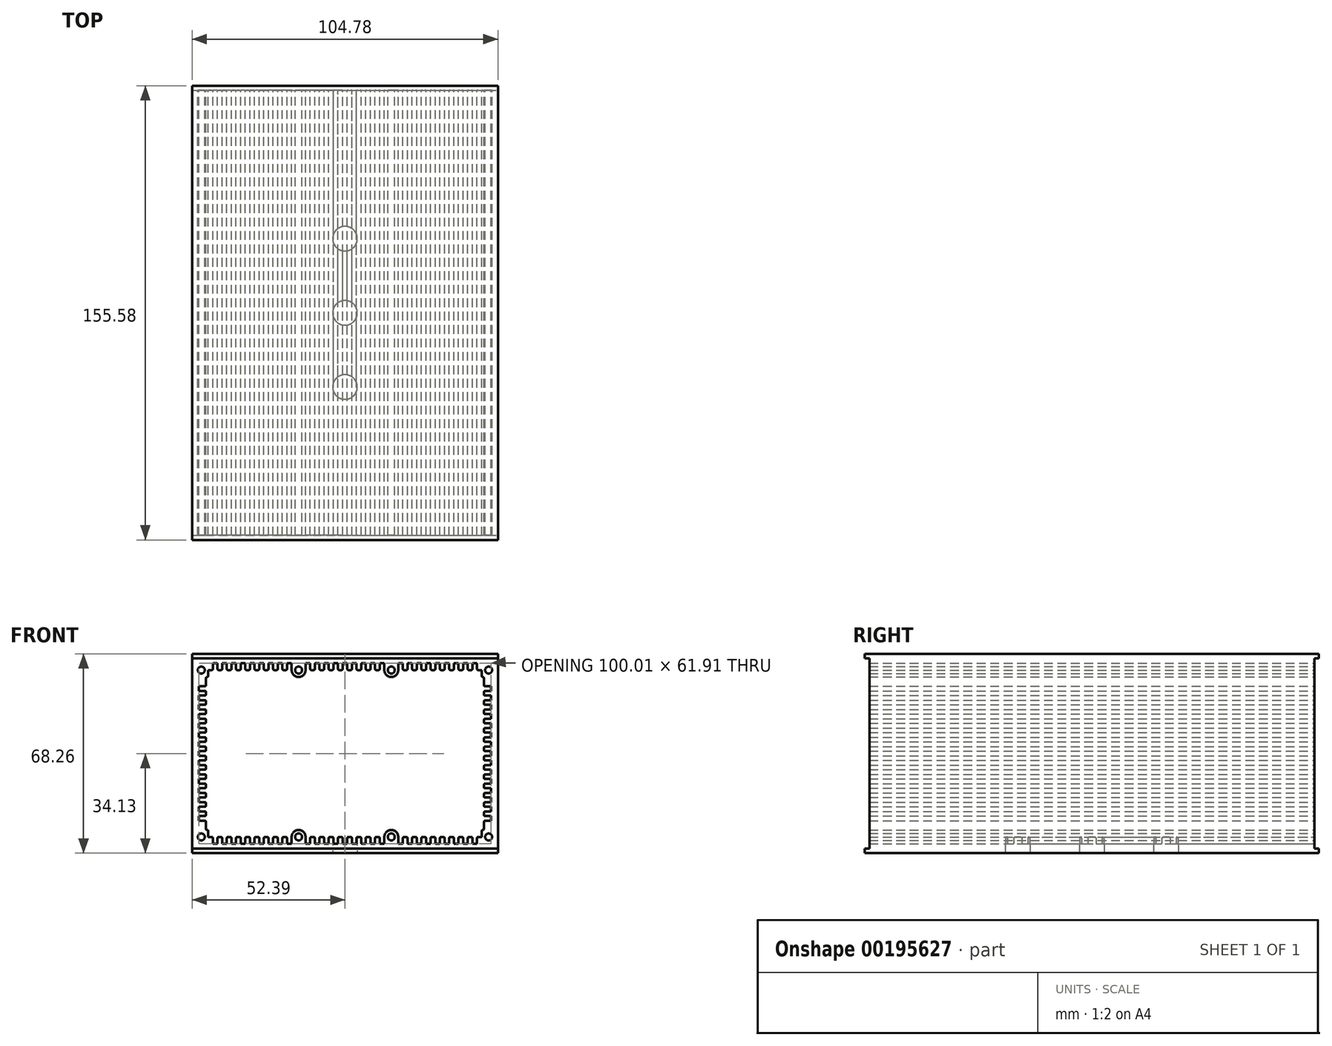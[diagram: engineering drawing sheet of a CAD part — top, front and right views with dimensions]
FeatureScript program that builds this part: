
annotation { "Feature Type Name" : "Feature", "Feature Type Description" : "" }
export const myFeature = defineFeature(function(context is Context, id is Id, definition is map)
    precondition{}
    {
        {
            var Q0;
            Q0=qCreatedBy(makeId("Front.planeOp"),FACE);
            var sketch = newSketch(context, id + "F0", { "sketchPlane" : qUnion([Q0])});
            skLineSegment(sketch, "E0.bottom", {"start": v(-52.39, 34.13) * mm, "end": v(52.39, 34.13) * mm});
            skLineSegment(sketch, "E0.top", {"start": v(-52.39, -34.13) * mm, "end": v(52.39, -34.13) * mm});
            skLineSegment(sketch, "E0.left", {"start": v(-52.39, 34.13) * mm, "end": v(-52.39, -34.13) * mm});
            skLineSegment(sketch, "E0.right", {"start": v(52.39, 34.13) * mm, "end": v(52.39, -34.13) * mm});
            skLineSegment(sketch, "E1.bottom", {"start": v(-50, 23.02) * mm, "end": v(-48.02, 23.02) * mm});
            skLineSegment(sketch, "E1.top", {"start": v(-50, 21.43) * mm, "end": v(-48.02, 21.43) * mm});
            skLineSegment(sketch, "E1.left", {"start": v(-50, 23.02) * mm, "end": v(-50, 21.43) * mm});
            skLineSegment(sketch, "E2", {"start": v(-47.62, 21.03) * mm, "end": v(-47.62, 20.24) * mm});
            skLineSegment(sketch, "E3.bottom", {"start": v(-50, 19.84) * mm, "end": v(-48.02, 19.84) * mm});
            skLineSegment(sketch, "E3.top", {"start": v(-50, 18.26) * mm, "end": v(-48.02, 18.26) * mm});
            skLineSegment(sketch, "E3.left", {"start": v(-50, 19.84) * mm, "end": v(-50, 18.26) * mm});
            skLineSegment(sketch, "E4", {"start": v(-47.62, 17.86) * mm, "end": v(-47.62, 17.07) * mm});
            skLineSegment(sketch, "E5.bottom", {"start": v(-50, 16.67) * mm, "end": v(-48.02, 16.67) * mm});
            skLineSegment(sketch, "E5.top", {"start": v(-50, 15.08) * mm, "end": v(-48.02, 15.08) * mm});
            skLineSegment(sketch, "E5.left", {"start": v(-50, 16.67) * mm, "end": v(-50, 15.08) * mm});
            skLineSegment(sketch, "E6", {"start": v(-47.62, 14.68) * mm, "end": v(-47.62, 13.9) * mm});
            skLineSegment(sketch, "E7.bottom", {"start": v(-50, 13.5) * mm, "end": v(-48.02, 13.5) * mm});
            skLineSegment(sketch, "E7.top", {"start": v(-50, 11.9) * mm, "end": v(-48.02, 11.9) * mm});
            skLineSegment(sketch, "E7.left", {"start": v(-50, 13.5) * mm, "end": v(-50, 11.9) * mm});
            skLineSegment(sketch, "E8", {"start": v(-47.62, 11.5) * mm, "end": v(-47.62, 10.72) * mm});
            skLineSegment(sketch, "E9.bottom", {"start": v(-50, 10.32) * mm, "end": v(-48.02, 10.32) * mm});
            skLineSegment(sketch, "E9.top", {"start": v(-50, 8.73) * mm, "end": v(-48.02, 8.73) * mm});
            skLineSegment(sketch, "E9.left", {"start": v(-50, 10.32) * mm, "end": v(-50, 8.73) * mm});
            skLineSegment(sketch, "E10", {"start": v(-47.62, 8.33) * mm, "end": v(-47.62, 7.54) * mm});
            skLineSegment(sketch, "E11.bottom", {"start": v(-50, 7.14) * mm, "end": v(-48.02, 7.14) * mm});
            skLineSegment(sketch, "E11.top", {"start": v(-50, 5.56) * mm, "end": v(-48.02, 5.56) * mm});
            skLineSegment(sketch, "E11.left", {"start": v(-50, 7.14) * mm, "end": v(-50, 5.56) * mm});
            skLineSegment(sketch, "E12", {"start": v(-47.62, 5.16) * mm, "end": v(-47.62, 4.37) * mm});
            skLineSegment(sketch, "E13.bottom", {"start": v(-50, 3.97) * mm, "end": v(-48.02, 3.97) * mm});
            skLineSegment(sketch, "E13.top", {"start": v(-50, 2.38) * mm, "end": v(-48.02, 2.38) * mm});
            skLineSegment(sketch, "E13.left", {"start": v(-50, 3.97) * mm, "end": v(-50, 2.38) * mm});
            skLineSegment(sketch, "E14", {"start": v(-47.62, 1.98) * mm, "end": v(-47.62, 1.2) * mm});
            skLineSegment(sketch, "E15.bottom", {"start": v(-50, 0.8) * mm, "end": v(-48.02, 0.8) * mm});
            skLineSegment(sketch, "E15.left", {"start": v(-50, 0.8) * mm, "end": v(-50, 0) * mm});
            skLineSegment(sketch, "E16.bottom", {"start": v(-43.66, 30.96) * mm, "end": v(-43.66, 28.97) * mm});
            skLineSegment(sketch, "E16.top", {"start": v(-45.24, 30.96) * mm, "end": v(-45.24, 28.97) * mm});
            skLineSegment(sketch, "E16.left", {"start": v(-43.66, 30.96) * mm, "end": v(-45.24, 30.96) * mm});
            skLineSegment(sketch, "E17", {"start": v(-45.64, 28.57) * mm, "end": v(-46.83, 28.57) * mm});
            skCircle(sketch, "E18", {"center": v(-49.21, 28.58) * mm, "radius": 1.2 * mm});
            skLineSegment(sketch, "E19", {"start": v(-47.62, 23.42) * mm, "end": v(-47.62, 25.8) * mm});
            skLineSegment(sketch, "E20", {"start": v(-46.83, 28.57) * mm, "end": v(-46.83, 26.6) * mm});
            skPoint(sketch, "E21.visualSharp", {"position": v(-47.62, 23.02) * mm});
            skArc(sketch, "E21.filletArc", {"start": v(-48.02, 23.02) * mm, "mid": v(-47.74, 23.13) * mm, "end": v(-47.62, 23.42) * mm});
            skPoint(sketch, "E22.visualSharp", {"position": v(-47.62, 21.43) * mm});
            skArc(sketch, "E22.filletArc", {"start": v(-47.62, 21.03) * mm, "mid": v(-47.74, 21.32) * mm, "end": v(-48.02, 21.43) * mm});
            skPoint(sketch, "E23.visualSharp", {"position": v(-47.62, 19.84) * mm});
            skArc(sketch, "E23.filletArc", {"start": v(-48.02, 19.84) * mm, "mid": v(-47.74, 19.96) * mm, "end": v(-47.62, 20.24) * mm});
            skPoint(sketch, "E24.visualSharp", {"position": v(-47.62, 18.26) * mm});
            skArc(sketch, "E24.filletArc", {"start": v(-47.62, 17.86) * mm, "mid": v(-47.74, 18.14) * mm, "end": v(-48.02, 18.26) * mm});
            skPoint(sketch, "E25.visualSharp", {"position": v(-47.62, 16.67) * mm});
            skArc(sketch, "E25.filletArc", {"start": v(-48.02, 16.67) * mm, "mid": v(-47.74, 16.78) * mm, "end": v(-47.62, 17.07) * mm});
            skPoint(sketch, "E26.visualSharp", {"position": v(-47.62, 15.08) * mm});
            skArc(sketch, "E26.filletArc", {"start": v(-47.62, 14.68) * mm, "mid": v(-47.74, 14.97) * mm, "end": v(-48.02, 15.08) * mm});
            skPoint(sketch, "E27.visualSharp", {"position": v(-47.62, 13.5) * mm});
            skArc(sketch, "E27.filletArc", {"start": v(-48.02, 13.5) * mm, "mid": v(-47.74, 13.6) * mm, "end": v(-47.62, 13.9) * mm});
            skPoint(sketch, "E28.visualSharp", {"position": v(-47.62, 11.9) * mm});
            skArc(sketch, "E28.filletArc", {"start": v(-47.62, 11.5) * mm, "mid": v(-47.74, 11.8) * mm, "end": v(-48.02, 11.9) * mm});
            skPoint(sketch, "E29.visualSharp", {"position": v(-47.62, 10.32) * mm});
            skArc(sketch, "E29.filletArc", {"start": v(-48.02, 10.32) * mm, "mid": v(-47.74, 10.43) * mm, "end": v(-47.62, 10.72) * mm});
            skPoint(sketch, "E30.visualSharp", {"position": v(-47.62, 8.73) * mm});
            skArc(sketch, "E30.filletArc", {"start": v(-47.62, 8.33) * mm, "mid": v(-47.74, 8.62) * mm, "end": v(-48.02, 8.73) * mm});
            skPoint(sketch, "E31.visualSharp", {"position": v(-47.62, 7.14) * mm});
            skArc(sketch, "E31.filletArc", {"start": v(-48.02, 7.14) * mm, "mid": v(-47.74, 7.26) * mm, "end": v(-47.62, 7.54) * mm});
            skPoint(sketch, "E32.visualSharp", {"position": v(-47.62, 5.56) * mm});
            skArc(sketch, "E32.filletArc", {"start": v(-47.62, 5.16) * mm, "mid": v(-47.74, 5.44) * mm, "end": v(-48.02, 5.56) * mm});
            skPoint(sketch, "E33.visualSharp", {"position": v(-47.62, 3.97) * mm});
            skArc(sketch, "E33.filletArc", {"start": v(-48.02, 3.97) * mm, "mid": v(-47.74, 4.08) * mm, "end": v(-47.62, 4.37) * mm});
            skPoint(sketch, "E34.visualSharp", {"position": v(-47.62, 2.38) * mm});
            skArc(sketch, "E34.filletArc", {"start": v(-47.62, 1.98) * mm, "mid": v(-47.74, 2.27) * mm, "end": v(-48.02, 2.38) * mm});
            skPoint(sketch, "E35.visualSharp", {"position": v(-47.62, 0.8) * mm});
            skArc(sketch, "E35.filletArc", {"start": v(-48.02, 0.8) * mm, "mid": v(-47.74, 0.9) * mm, "end": v(-47.62, 1.2) * mm});
            skPoint(sketch, "E36.visualSharp", {"position": v(-45.24, 28.57) * mm});
            skArc(sketch, "E36.filletArc", {"start": v(-45.64, 28.58) * mm, "mid": v(-45.36, 28.7) * mm, "end": v(-45.24, 28.97) * mm});
            skLineSegment(sketch, "E37.top", {"start": v(-42.07, 30.96) * mm, "end": v(-42.07, 28.97) * mm});
            skLineSegment(sketch, "E37.left", {"start": v(-40.48, 30.96) * mm, "end": v(-42.07, 30.96) * mm});
            skLineSegment(sketch, "E38", {"start": v(-42.47, 28.58) * mm, "end": v(-43.26, 28.58) * mm});
            skPoint(sketch, "E39.visualSharp", {"position": v(-42.07, 28.57) * mm});
            skArc(sketch, "E39.filletArc", {"start": v(-42.47, 28.58) * mm, "mid": v(-42.18, 28.7) * mm, "end": v(-42.07, 28.97) * mm});
            skPoint(sketch, "E40.visualSharp", {"position": v(-43.66, 28.58) * mm});
            skArc(sketch, "E40.filletArc", {"start": v(-43.66, 28.97) * mm, "mid": v(-43.54, 28.7) * mm, "end": v(-43.26, 28.58) * mm});
            skLineSegment(sketch, "E41.bottom", {"start": v(-40.48, 30.96) * mm, "end": v(-40.48, 28.97) * mm});
            skLineSegment(sketch, "E42.top", {"start": v(-38.9, 30.96) * mm, "end": v(-38.9, 28.97) * mm});
            skLineSegment(sketch, "E42.left", {"start": v(-37.3, 30.96) * mm, "end": v(-38.9, 30.96) * mm});
            skLineSegment(sketch, "E43", {"start": v(-39.3, 28.58) * mm, "end": v(-40.08, 28.58) * mm});
            skPoint(sketch, "E44.visualSharp", {"position": v(-38.9, 28.58) * mm});
            skArc(sketch, "E44.filletArc", {"start": v(-39.3, 28.58) * mm, "mid": v(-39, 28.7) * mm, "end": v(-38.9, 28.97) * mm});
            skPoint(sketch, "E45.visualSharp", {"position": v(-40.48, 28.58) * mm});
            skArc(sketch, "E45.filletArc", {"start": v(-40.48, 28.97) * mm, "mid": v(-40.37, 28.7) * mm, "end": v(-40.08, 28.58) * mm});
            skLineSegment(sketch, "E46.bottom", {"start": v(-37.3, 30.96) * mm, "end": v(-37.3, 28.97) * mm});
            skLineSegment(sketch, "E47.top", {"start": v(-35.72, 30.96) * mm, "end": v(-35.72, 28.97) * mm});
            skLineSegment(sketch, "E47.left", {"start": v(-34.13, 30.96) * mm, "end": v(-35.72, 30.96) * mm});
            skLineSegment(sketch, "E48", {"start": v(-36.12, 28.58) * mm, "end": v(-36.9, 28.58) * mm});
            skPoint(sketch, "E49.visualSharp", {"position": v(-35.72, 28.58) * mm});
            skArc(sketch, "E49.filletArc", {"start": v(-36.12, 28.58) * mm, "mid": v(-35.83, 28.7) * mm, "end": v(-35.72, 28.97) * mm});
            skPoint(sketch, "E50.visualSharp", {"position": v(-37.3, 28.58) * mm});
            skArc(sketch, "E50.filletArc", {"start": v(-37.3, 28.97) * mm, "mid": v(-37.2, 28.7) * mm, "end": v(-36.9, 28.58) * mm});
            skLineSegment(sketch, "E51.bottom", {"start": v(-34.13, 30.96) * mm, "end": v(-34.13, 28.97) * mm});
            skLineSegment(sketch, "E52.top", {"start": v(-32.54, 30.96) * mm, "end": v(-32.54, 28.97) * mm});
            skLineSegment(sketch, "E52.left", {"start": v(-30.96, 30.96) * mm, "end": v(-32.54, 30.96) * mm});
            skLineSegment(sketch, "E53", {"start": v(-32.94, 28.58) * mm, "end": v(-33.73, 28.58) * mm});
            skPoint(sketch, "E54.visualSharp", {"position": v(-32.54, 28.58) * mm});
            skArc(sketch, "E54.filletArc", {"start": v(-32.94, 28.58) * mm, "mid": v(-32.66, 28.7) * mm, "end": v(-32.54, 28.97) * mm});
            skPoint(sketch, "E55.visualSharp", {"position": v(-34.13, 28.58) * mm});
            skArc(sketch, "E55.filletArc", {"start": v(-34.13, 28.97) * mm, "mid": v(-34.02, 28.7) * mm, "end": v(-33.73, 28.58) * mm});
            skLineSegment(sketch, "E56.bottom", {"start": v(-30.96, 30.96) * mm, "end": v(-30.96, 28.97) * mm});
            skLineSegment(sketch, "E57.top", {"start": v(-29.37, 30.96) * mm, "end": v(-29.37, 28.97) * mm});
            skLineSegment(sketch, "E57.left", {"start": v(-27.78, 30.96) * mm, "end": v(-29.37, 30.96) * mm});
            skLineSegment(sketch, "E58", {"start": v(-29.77, 28.58) * mm, "end": v(-30.56, 28.58) * mm});
            skPoint(sketch, "E59.visualSharp", {"position": v(-29.37, 28.58) * mm});
            skArc(sketch, "E59.filletArc", {"start": v(-29.77, 28.58) * mm, "mid": v(-29.48, 28.7) * mm, "end": v(-29.37, 28.97) * mm});
            skArc(sketch, "E60.filletArc", {"start": v(-30.96, 28.97) * mm, "mid": v(-30.84, 28.7) * mm, "end": v(-30.56, 28.58) * mm});
            skLineSegment(sketch, "E61.bottom", {"start": v(-27.78, 30.96) * mm, "end": v(-27.78, 28.97) * mm});
            skLineSegment(sketch, "E62.top", {"start": v(-26.2, 30.96) * mm, "end": v(-26.2, 28.97) * mm});
            skLineSegment(sketch, "E62.left", {"start": v(-24.6, 30.96) * mm, "end": v(-26.2, 30.96) * mm});
            skLineSegment(sketch, "E63", {"start": v(-26.6, 28.58) * mm, "end": v(-27.38, 28.58) * mm});
            skPoint(sketch, "E64.visualSharp", {"position": v(-26.2, 28.58) * mm});
            skArc(sketch, "E64.filletArc", {"start": v(-26.6, 28.58) * mm, "mid": v(-26.3, 28.7) * mm, "end": v(-26.2, 28.97) * mm});
            skPoint(sketch, "E65.visualSharp", {"position": v(-27.78, 28.58) * mm});
            skArc(sketch, "E65.filletArc", {"start": v(-27.78, 28.97) * mm, "mid": v(-27.67, 28.7) * mm, "end": v(-27.38, 28.58) * mm});
            skLineSegment(sketch, "E66.bottom", {"start": v(-24.6, 30.96) * mm, "end": v(-24.6, 28.97) * mm});
            skLineSegment(sketch, "E67.top", {"start": v(-23.02, 30.96) * mm, "end": v(-23.02, 28.97) * mm});
            skLineSegment(sketch, "E67.left", {"start": v(-21.43, 30.96) * mm, "end": v(-23.02, 30.96) * mm});
            skLineSegment(sketch, "E68", {"start": v(-23.42, 28.58) * mm, "end": v(-24.2, 28.58) * mm});
            skPoint(sketch, "E69.visualSharp", {"position": v(-23.02, 28.58) * mm});
            skArc(sketch, "E69.filletArc", {"start": v(-23.42, 28.58) * mm, "mid": v(-23.13, 28.7) * mm, "end": v(-23.02, 28.97) * mm});
            skPoint(sketch, "E70.visualSharp", {"position": v(-24.6, 28.58) * mm});
            skArc(sketch, "E70.filletArc", {"start": v(-24.6, 28.97) * mm, "mid": v(-24.5, 28.7) * mm, "end": v(-24.2, 28.58) * mm});
            skLineSegment(sketch, "E71.bottom", {"start": v(-21.43, 30.96) * mm, "end": v(-21.43, 28.97) * mm});
            skLineSegment(sketch, "E72.top", {"start": v(-19.84, 30.96) * mm, "end": v(-19.84, 28.97) * mm});
            skLineSegment(sketch, "E72.left", {"start": v(-18.26, 30.96) * mm, "end": v(-19.84, 30.96) * mm});
            skLineSegment(sketch, "E73", {"start": v(-20.24, 28.58) * mm, "end": v(-21.03, 28.58) * mm});
            skPoint(sketch, "E74.visualSharp", {"position": v(-19.84, 28.58) * mm});
            skArc(sketch, "E74.filletArc", {"start": v(-20.24, 28.58) * mm, "mid": v(-19.96, 28.7) * mm, "end": v(-19.84, 28.97) * mm});
            skArc(sketch, "E75.filletArc", {"start": v(-21.43, 28.97) * mm, "mid": v(-21.32, 28.7) * mm, "end": v(-21.03, 28.58) * mm});
            skLineSegment(sketch, "E76.bottom", {"start": v(-18.26, 30.96) * mm, "end": v(-18.26, 28.58) * mm});
            skLineSegment(sketch, "E77.top", {"start": v(-13.5, 30.96) * mm, "end": v(-13.5, 28.58) * mm});
            skLineSegment(sketch, "E77.left", {"start": v(-11.9, 30.96) * mm, "end": v(-13.5, 30.96) * mm});
            skLineSegment(sketch, "E78.bottom", {"start": v(-11.9, 30.96) * mm, "end": v(-11.9, 28.97) * mm});
            skLineSegment(sketch, "E79.top", {"start": v(-10.32, 30.96) * mm, "end": v(-10.32, 28.97) * mm});
            skLineSegment(sketch, "E79.left", {"start": v(-8.73, 30.96) * mm, "end": v(-10.32, 30.96) * mm});
            skLineSegment(sketch, "E80", {"start": v(-10.72, 28.57) * mm, "end": v(-11.5, 28.57) * mm});
            skPoint(sketch, "E81.visualSharp", {"position": v(-10.32, 28.57) * mm});
            skArc(sketch, "E81.filletArc", {"start": v(-10.72, 28.57) * mm, "mid": v(-10.43, 28.7) * mm, "end": v(-10.32, 28.97) * mm});
            skPoint(sketch, "E82.visualSharp", {"position": v(-11.9, 28.57) * mm});
            skArc(sketch, "E82.filletArc", {"start": v(-11.9, 28.97) * mm, "mid": v(-11.8, 28.7) * mm, "end": v(-11.5, 28.57) * mm});
            skLineSegment(sketch, "E83.bottom", {"start": v(-8.73, 30.96) * mm, "end": v(-8.73, 28.97) * mm});
            skLineSegment(sketch, "E84.top", {"start": v(-7.14, 30.96) * mm, "end": v(-7.14, 28.97) * mm});
            skLineSegment(sketch, "E84.left", {"start": v(-5.56, 30.96) * mm, "end": v(-7.14, 30.96) * mm});
            skLineSegment(sketch, "E85", {"start": v(-7.54, 28.57) * mm, "end": v(-8.33, 28.57) * mm});
            skPoint(sketch, "E86.visualSharp", {"position": v(-7.14, 28.57) * mm});
            skArc(sketch, "E86.filletArc", {"start": v(-7.54, 28.57) * mm, "mid": v(-7.26, 28.7) * mm, "end": v(-7.14, 28.97) * mm});
            skPoint(sketch, "E87.visualSharp", {"position": v(-8.73, 28.57) * mm});
            skArc(sketch, "E87.filletArc", {"start": v(-8.73, 28.97) * mm, "mid": v(-8.62, 28.7) * mm, "end": v(-8.33, 28.57) * mm});
            skLineSegment(sketch, "E88.bottom", {"start": v(-5.56, 30.96) * mm, "end": v(-5.56, 28.97) * mm});
            skLineSegment(sketch, "E89.top", {"start": v(-3.97, 30.96) * mm, "end": v(-3.97, 28.97) * mm});
            skLineSegment(sketch, "E89.left", {"start": v(-2.38, 30.96) * mm, "end": v(-3.97, 30.96) * mm});
            skLineSegment(sketch, "E90", {"start": v(-4.37, 28.57) * mm, "end": v(-5.16, 28.57) * mm});
            skPoint(sketch, "E91.visualSharp", {"position": v(-3.97, 28.57) * mm});
            skArc(sketch, "E91.filletArc", {"start": v(-4.37, 28.57) * mm, "mid": v(-4.08, 28.7) * mm, "end": v(-3.97, 28.97) * mm});
            skPoint(sketch, "E92.visualSharp", {"position": v(-5.56, 28.57) * mm});
            skArc(sketch, "E92.filletArc", {"start": v(-5.56, 28.97) * mm, "mid": v(-5.44, 28.7) * mm, "end": v(-5.16, 28.57) * mm});
            skLineSegment(sketch, "E93.bottom", {"start": v(-2.38, 30.96) * mm, "end": v(-2.38, 28.97) * mm});
            skLineSegment(sketch, "E94.top", {"start": v(-0.8, 30.96) * mm, "end": v(-0.8, 28.97) * mm});
            skLineSegment(sketch, "E95", {"start": v(-1.2, 28.57) * mm, "end": v(-1.98, 28.57) * mm});
            skPoint(sketch, "E96.visualSharp", {"position": v(-0.8, 28.57) * mm});
            skArc(sketch, "E96.filletArc", {"start": v(-1.2, 28.57) * mm, "mid": v(-0.9, 28.7) * mm, "end": v(-0.8, 28.97) * mm});
            skPoint(sketch, "E97.visualSharp", {"position": v(-2.38, 28.57) * mm});
            skArc(sketch, "E97.filletArc", {"start": v(-2.38, 28.97) * mm, "mid": v(-2.27, 28.7) * mm, "end": v(-1.98, 28.57) * mm});
            skLineSegment(sketch, "E98", {"start": v(0, 30.96) * mm, "end": v(-0.8, 30.96) * mm});
            skCircle(sketch, "E99", {"center": v(-15.88, 28.57) * mm, "radius": 1.2 * mm});
            skLineSegment(sketch, "E100", {"start": v(-47.23, 26.2) * mm, "end": v(-47.23, 26.2) * mm});
            skPoint(sketch, "E101.visualSharp", {"position": v(-47.62, 26.2) * mm});
            skArc(sketch, "E101.filletArc", {"start": v(-47.23, 26.2) * mm, "mid": v(-47.5, 26.08) * mm, "end": v(-47.62, 25.8) * mm});
            skPoint(sketch, "E102.visualSharp", {"position": v(-46.83, 26.2) * mm});
            skArc(sketch, "E102.filletArc", {"start": v(-47.23, 26.2) * mm, "mid": v(-46.95, 26.3) * mm, "end": v(-46.83, 26.6) * mm});
            skArc(sketch, "E103", {"start": v(-18.26, 28.58) * mm, "mid": v(-15.88, 26.2) * mm, "end": v(-13.5, 28.58) * mm});
            skArc(sketch, "E104.MirrorCS", {"start": v(47.23, 26.2) * mm, "mid": v(46.95, 26.3) * mm, "end": v(46.83, 26.6) * mm});
            skArc(sketch, "E105.MirrorCS", {"start": v(29.77, 28.58) * mm, "mid": v(29.48, 28.7) * mm, "end": v(29.37, 28.97) * mm});
            skArc(sketch, "E106.MirrorCS", {"start": v(48.02, 10.32) * mm, "mid": v(47.74, 10.43) * mm, "end": v(47.62, 10.72) * mm});
            skLineSegment(sketch, "E107.MirrorCS", {"start": v(47.62, 11.5) * mm, "end": v(47.62, 10.72) * mm});
            skArc(sketch, "E108.MirrorCS", {"start": v(23.42, 28.58) * mm, "mid": v(23.13, 28.7) * mm, "end": v(23.02, 28.97) * mm});
            skLineSegment(sketch, "E109.MirrorCS", {"start": v(1.2, 28.57) * mm, "end": v(1.98, 28.57) * mm});
            skLineSegment(sketch, "E110.MirrorCS", {"start": v(42.47, 28.58) * mm, "end": v(43.26, 28.58) * mm});
            skLineSegment(sketch, "E111.MirrorCS", {"start": v(29.77, 28.58) * mm, "end": v(30.56, 28.58) * mm});
            skLineSegment(sketch, "E112.MirrorCS", {"start": v(47.62, 14.68) * mm, "end": v(47.62, 13.9) * mm});
            skLineSegment(sketch, "E113.MirrorCS", {"start": v(23.42, 28.58) * mm, "end": v(24.2, 28.58) * mm});
            skArc(sketch, "E114.MirrorCS", {"start": v(48.02, 13.5) * mm, "mid": v(47.74, 13.6) * mm, "end": v(47.62, 13.9) * mm});
            skArc(sketch, "E115.MirrorCS", {"start": v(47.23, 26.2) * mm, "mid": v(47.5, 26.08) * mm, "end": v(47.62, 25.8) * mm});
            skArc(sketch, "E116.MirrorCS", {"start": v(42.47, 28.58) * mm, "mid": v(42.18, 28.7) * mm, "end": v(42.07, 28.97) * mm});
            skArc(sketch, "E117.MirrorCS", {"start": v(2.38, 28.97) * mm, "mid": v(2.27, 28.7) * mm, "end": v(1.98, 28.57) * mm});
            skArc(sketch, "E118.MirrorCS", {"start": v(20.24, 28.58) * mm, "mid": v(19.96, 28.7) * mm, "end": v(19.84, 28.97) * mm});
            skArc(sketch, "E119.MirrorCS", {"start": v(5.56, 28.97) * mm, "mid": v(5.44, 28.7) * mm, "end": v(5.16, 28.57) * mm});
            skArc(sketch, "E120.MirrorCS", {"start": v(10.72, 28.57) * mm, "mid": v(10.43, 28.7) * mm, "end": v(10.32, 28.97) * mm});
            skLineSegment(sketch, "E121.MirrorCS", {"start": v(20.24, 28.58) * mm, "end": v(21.03, 28.58) * mm});
            skArc(sketch, "E122.MirrorCS", {"start": v(7.54, 28.57) * mm, "mid": v(7.26, 28.7) * mm, "end": v(7.14, 28.97) * mm});
            skArc(sketch, "E123.MirrorCS", {"start": v(43.66, 28.97) * mm, "mid": v(43.54, 28.7) * mm, "end": v(43.26, 28.58) * mm});
            skArc(sketch, "E124.MirrorCS", {"start": v(48.02, 16.67) * mm, "mid": v(47.74, 16.78) * mm, "end": v(47.62, 17.07) * mm});
            skArc(sketch, "E125.MirrorCS", {"start": v(47.62, 5.16) * mm, "mid": v(47.74, 5.44) * mm, "end": v(48.02, 5.56) * mm});
            skArc(sketch, "E126.MirrorCS", {"start": v(47.62, 21.03) * mm, "mid": v(47.74, 21.32) * mm, "end": v(48.02, 21.43) * mm});
            skLineSegment(sketch, "E127.MirrorCS", {"start": v(26.6, 28.58) * mm, "end": v(27.38, 28.58) * mm});
            skArc(sketch, "E128.MirrorCS", {"start": v(48.02, 23.02) * mm, "mid": v(47.74, 23.13) * mm, "end": v(47.62, 23.42) * mm});
            skArc(sketch, "E129.MirrorCS", {"start": v(24.6, 28.97) * mm, "mid": v(24.5, 28.7) * mm, "end": v(24.2, 28.58) * mm});
            skArc(sketch, "E130.MirrorCS", {"start": v(26.6, 28.58) * mm, "mid": v(26.3, 28.7) * mm, "end": v(26.2, 28.97) * mm});
            skLineSegment(sketch, "E131.MirrorCS", {"start": v(0, 30.96) * mm, "end": v(0.8, 30.96) * mm});
            skLineSegment(sketch, "E132.MirrorCS", {"start": v(50, 0.8) * mm, "end": v(50, 0) * mm});
            skArc(sketch, "E133.MirrorCS", {"start": v(36.12, 28.58) * mm, "mid": v(35.83, 28.7) * mm, "end": v(35.72, 28.97) * mm});
            skLineSegment(sketch, "E134.MirrorCS", {"start": v(36.12, 28.58) * mm, "end": v(36.9, 28.58) * mm});
            skArc(sketch, "E135.MirrorCS", {"start": v(21.43, 28.97) * mm, "mid": v(21.32, 28.7) * mm, "end": v(21.03, 28.58) * mm});
            skLineSegment(sketch, "E136.MirrorCS", {"start": v(47.62, 17.86) * mm, "end": v(47.62, 17.07) * mm});
            skLineSegment(sketch, "E137.MirrorCS", {"start": v(21.43, 30.96) * mm, "end": v(23.02, 30.96) * mm});
            skLineSegment(sketch, "E138.MirrorCS", {"start": v(10.72, 28.57) * mm, "end": v(11.5, 28.57) * mm});
            skLineSegment(sketch, "E139.MirrorCS", {"start": v(7.54, 28.57) * mm, "end": v(8.33, 28.57) * mm});
            skLineSegment(sketch, "E140.MirrorCS", {"start": v(32.94, 28.58) * mm, "end": v(33.73, 28.58) * mm});
            skArc(sketch, "E141.MirrorCS", {"start": v(27.78, 28.97) * mm, "mid": v(27.67, 28.7) * mm, "end": v(27.38, 28.57) * mm});
            skArc(sketch, "E142.MirrorCS", {"start": v(4.37, 28.57) * mm, "mid": v(4.08, 28.7) * mm, "end": v(3.97, 28.97) * mm});
            skArc(sketch, "E143.MirrorCS", {"start": v(48.02, 19.84) * mm, "mid": v(47.74, 19.96) * mm, "end": v(47.62, 20.24) * mm});
            skLineSegment(sketch, "E144.MirrorCS", {"start": v(47.62, 5.16) * mm, "end": v(47.62, 4.37) * mm});
            skArc(sketch, "E145.MirrorCS", {"start": v(40.48, 28.97) * mm, "mid": v(40.37, 28.7) * mm, "end": v(40.08, 28.58) * mm});
            skArc(sketch, "E146.MirrorCS", {"start": v(48.02, 7.14) * mm, "mid": v(47.74, 7.26) * mm, "end": v(47.62, 7.54) * mm});
            skLineSegment(sketch, "E147.MirrorCS", {"start": v(4.37, 28.57) * mm, "end": v(5.16, 28.57) * mm});
            skArc(sketch, "E148.MirrorCS", {"start": v(39.3, 28.58) * mm, "mid": v(39, 28.7) * mm, "end": v(38.9, 28.97) * mm});
            skArc(sketch, "E149.MirrorCS", {"start": v(47.62, 8.33) * mm, "mid": v(47.74, 8.62) * mm, "end": v(48.02, 8.73) * mm});
            skArc(sketch, "E150.MirrorCS", {"start": v(37.3, 28.97) * mm, "mid": v(37.2, 28.7) * mm, "end": v(36.9, 28.57) * mm});
            skArc(sketch, "E151.MirrorCS", {"start": v(45.64, 28.58) * mm, "mid": v(45.36, 28.7) * mm, "end": v(45.24, 28.97) * mm});
            skArc(sketch, "E152.MirrorCS", {"start": v(47.62, 11.5) * mm, "mid": v(47.74, 11.8) * mm, "end": v(48.02, 11.9) * mm});
            skLineSegment(sketch, "E153.MirrorCS", {"start": v(47.62, 21.03) * mm, "end": v(47.62, 20.24) * mm});
            skArc(sketch, "E154.MirrorCS", {"start": v(8.73, 28.97) * mm, "mid": v(8.62, 28.7) * mm, "end": v(8.33, 28.57) * mm});
            skLineSegment(sketch, "E155.MirrorCS", {"start": v(47.62, 1.98) * mm, "end": v(47.62, 1.2) * mm});
            skArc(sketch, "E156.MirrorCS", {"start": v(47.62, 1.98) * mm, "mid": v(47.74, 2.27) * mm, "end": v(48.02, 2.38) * mm});
            skArc(sketch, "E157.MirrorCS", {"start": v(34.13, 28.97) * mm, "mid": v(34.02, 28.7) * mm, "end": v(33.73, 28.58) * mm});
            skLineSegment(sketch, "E158.MirrorCS", {"start": v(45.64, 28.57) * mm, "end": v(46.83, 28.57) * mm});
            skArc(sketch, "E159.MirrorCS", {"start": v(47.62, 14.68) * mm, "mid": v(47.74, 14.97) * mm, "end": v(48.02, 15.08) * mm});
            skArc(sketch, "E160.MirrorCS", {"start": v(48.02, 3.97) * mm, "mid": v(47.74, 4.08) * mm, "end": v(47.62, 4.37) * mm});
            skArc(sketch, "E161.MirrorCS", {"start": v(30.96, 28.97) * mm, "mid": v(30.84, 28.7) * mm, "end": v(30.56, 28.58) * mm});
            skArc(sketch, "E162.MirrorCS", {"start": v(32.94, 28.58) * mm, "mid": v(32.66, 28.7) * mm, "end": v(32.54, 28.97) * mm});
            skArc(sketch, "E163.MirrorCS", {"start": v(47.62, 17.86) * mm, "mid": v(47.74, 18.14) * mm, "end": v(48.02, 18.26) * mm});
            skLineSegment(sketch, "E164.MirrorCS", {"start": v(39.3, 28.58) * mm, "end": v(40.08, 28.58) * mm});
            skLineSegment(sketch, "E165.MirrorCS", {"start": v(24.6, 30.96) * mm, "end": v(26.2, 30.96) * mm});
            skArc(sketch, "E166.MirrorCS", {"start": v(1.2, 28.57) * mm, "mid": v(0.9, 28.7) * mm, "end": v(0.8, 28.97) * mm});
            skArc(sketch, "E167.MirrorCS", {"start": v(11.9, 28.97) * mm, "mid": v(11.8, 28.7) * mm, "end": v(11.5, 28.57) * mm});
            skArc(sketch, "E168.MirrorCS", {"start": v(48.02, 0.8) * mm, "mid": v(47.74, 0.9) * mm, "end": v(47.62, 1.2) * mm});
            skLineSegment(sketch, "E169.MirrorCS", {"start": v(47.62, 8.33) * mm, "end": v(47.62, 7.54) * mm});
            skLineSegment(sketch, "E170.MirrorCS", {"start": v(30.96, 30.96) * mm, "end": v(32.54, 30.96) * mm});
            skLineSegment(sketch, "E171.MirrorCS", {"start": v(18.26, 30.96) * mm, "end": v(19.84, 30.96) * mm});
            skLineSegment(sketch, "E172.MirrorCS", {"start": v(43.66, 30.96) * mm, "end": v(45.24, 30.96) * mm});
            skLineSegment(sketch, "E173.MirrorCS", {"start": v(2.38, 30.96) * mm, "end": v(3.97, 30.96) * mm});
            skLineSegment(sketch, "E174.MirrorCS", {"start": v(8.73, 30.96) * mm, "end": v(10.32, 30.96) * mm});
            skLineSegment(sketch, "E175.MirrorCS", {"start": v(5.56, 30.96) * mm, "end": v(7.14, 30.96) * mm});
            skLineSegment(sketch, "E176.MirrorCS", {"start": v(11.9, 30.96) * mm, "end": v(13.5, 30.96) * mm});
            skLineSegment(sketch, "E177.MirrorCS", {"start": v(50, 7.14) * mm, "end": v(50, 5.56) * mm});
            skLineSegment(sketch, "E178.MirrorCS", {"start": v(40.48, 30.96) * mm, "end": v(42.07, 30.96) * mm});
            skLineSegment(sketch, "E179.MirrorCS", {"start": v(27.78, 30.96) * mm, "end": v(29.37, 30.96) * mm});
            skLineSegment(sketch, "E180.MirrorCS", {"start": v(50, 13.5) * mm, "end": v(50, 11.9) * mm});
            skLineSegment(sketch, "E181.MirrorCS", {"start": v(50, 23.02) * mm, "end": v(50, 21.43) * mm});
            skLineSegment(sketch, "E182.MirrorCS", {"start": v(50, 16.67) * mm, "end": v(50, 15.08) * mm});
            skLineSegment(sketch, "E183.MirrorCS", {"start": v(34.13, 30.96) * mm, "end": v(35.72, 30.96) * mm});
            skLineSegment(sketch, "E184.MirrorCS", {"start": v(50, 10.32) * mm, "end": v(50, 8.73) * mm});
            skLineSegment(sketch, "E185.MirrorCS", {"start": v(50, 3.97) * mm, "end": v(50, 2.38) * mm});
            skLineSegment(sketch, "E186.MirrorCS", {"start": v(37.3, 30.96) * mm, "end": v(38.9, 30.96) * mm});
            skLineSegment(sketch, "E187.MirrorCS", {"start": v(50, 19.84) * mm, "end": v(50, 18.26) * mm});
            skLineSegment(sketch, "E188.MirrorCS", {"start": v(50, 19.84) * mm, "end": v(48.02, 19.84) * mm});
            skPoint(sketch, "E189.MirrorP", {"position": v(47.62, 21.43) * mm});
            skPoint(sketch, "E190.MirrorP", {"position": v(24.6, 28.58) * mm});
            skPoint(sketch, "E191.MirrorP", {"position": v(29.37, 28.58) * mm});
            skLineSegment(sketch, "E192.MirrorCS", {"start": v(3.97, 30.96) * mm, "end": v(3.97, 28.97) * mm});
            skPoint(sketch, "E193.MirrorP", {"position": v(43.66, 28.58) * mm});
            skLineSegment(sketch, "E194.MirrorCS", {"start": v(50, 15.08) * mm, "end": v(48.02, 15.08) * mm});
            skLineSegment(sketch, "E195.MirrorCS", {"start": v(50, 23.02) * mm, "end": v(48.02, 23.02) * mm});
            skLineSegment(sketch, "E196.MirrorCS", {"start": v(50, 8.73) * mm, "end": v(48.02, 8.73) * mm});
            skLineSegment(sketch, "E197.MirrorCS", {"start": v(24.6, 30.96) * mm, "end": v(24.6, 28.97) * mm});
            skPoint(sketch, "E198.MirrorP", {"position": v(10.32, 28.57) * mm});
            skPoint(sketch, "E199.MirrorP", {"position": v(45.24, 28.57) * mm});
            skPoint(sketch, "E200.MirrorP", {"position": v(47.62, 11.9) * mm});
            skLineSegment(sketch, "E201.MirrorCS", {"start": v(23.02, 30.96) * mm, "end": v(23.02, 28.97) * mm});
            skLineSegment(sketch, "E202.MirrorCS", {"start": v(2.38, 30.96) * mm, "end": v(2.38, 28.97) * mm});
            skPoint(sketch, "E203.MirrorP", {"position": v(34.13, 28.58) * mm});
            skLineSegment(sketch, "E204.MirrorCS", {"start": v(37.3, 30.96) * mm, "end": v(37.3, 28.97) * mm});
            skPoint(sketch, "E205.MirrorP", {"position": v(42.07, 28.57) * mm});
            skPoint(sketch, "E206.MirrorP", {"position": v(23.02, 28.58) * mm});
            skLineSegment(sketch, "E207.MirrorCS", {"start": v(19.84, 30.96) * mm, "end": v(19.84, 28.97) * mm});
            skPoint(sketch, "E208.MirrorP", {"position": v(3.97, 28.57) * mm});
            skPoint(sketch, "E209.MirrorP", {"position": v(47.62, 5.56) * mm});
            skPoint(sketch, "E210.MirrorP", {"position": v(47.62, 18.26) * mm});
            skPoint(sketch, "E211.MirrorP", {"position": v(40.48, 28.58) * mm});
            skLineSegment(sketch, "E212.MirrorCS", {"start": v(34.13, 30.96) * mm, "end": v(34.13, 28.97) * mm});
            skLineSegment(sketch, "E213.MirrorCS", {"start": v(21.43, 30.96) * mm, "end": v(21.43, 28.97) * mm});
            skLineSegment(sketch, "E214.MirrorCS", {"start": v(7.14, 30.96) * mm, "end": v(7.14, 28.97) * mm});
            skLineSegment(sketch, "E215.MirrorCS", {"start": v(43.66, 30.96) * mm, "end": v(43.66, 28.97) * mm});
            skPoint(sketch, "E216.MirrorP", {"position": v(27.78, 28.58) * mm});
            skPoint(sketch, "E217.MirrorP", {"position": v(32.54, 28.58) * mm});
            skPoint(sketch, "E218.MirrorP", {"position": v(47.62, 13.5) * mm});
            skPoint(sketch, "E219.MirrorP", {"position": v(8.73, 28.57) * mm});
            skLineSegment(sketch, "E220.MirrorCS", {"start": v(29.37, 30.96) * mm, "end": v(29.37, 28.97) * mm});
            skPoint(sketch, "E221.MirrorP", {"position": v(47.62, 7.14) * mm});
            skLineSegment(sketch, "E222.MirrorCS", {"start": v(50, 0.8) * mm, "end": v(48.02, 0.8) * mm});
            skLineSegment(sketch, "E223.MirrorCS", {"start": v(47.62, 23.42) * mm, "end": v(47.62, 25.8) * mm});
            skLineSegment(sketch, "E224.MirrorCS", {"start": v(5.56, 30.96) * mm, "end": v(5.56, 28.97) * mm});
            skPoint(sketch, "E225.MirrorP", {"position": v(0.8, 28.57) * mm});
            skLineSegment(sketch, "E226.MirrorCS", {"start": v(50, 16.67) * mm, "end": v(48.02, 16.67) * mm});
            skPoint(sketch, "E227.MirrorP", {"position": v(47.62, 8.73) * mm});
            skPoint(sketch, "E228.MirrorP", {"position": v(47.62, 26.2) * mm});
            skLineSegment(sketch, "E229.MirrorCS", {"start": v(50, 2.38) * mm, "end": v(48.02, 2.38) * mm});
            skLineSegment(sketch, "E230.MirrorCS", {"start": v(50, 10.32) * mm, "end": v(48.02, 10.32) * mm});
            skLineSegment(sketch, "E231.MirrorCS", {"start": v(32.54, 30.96) * mm, "end": v(32.54, 28.97) * mm});
            skPoint(sketch, "E232.MirrorP", {"position": v(11.9, 28.57) * mm});
            skLineSegment(sketch, "E233.MirrorCS", {"start": v(11.9, 30.96) * mm, "end": v(11.9, 28.97) * mm});
            skPoint(sketch, "E234.MirrorP", {"position": v(47.62, 23.02) * mm});
            skPoint(sketch, "E235.MirrorP", {"position": v(47.62, 10.32) * mm});
            skLineSegment(sketch, "E236.MirrorCS", {"start": v(45.24, 30.96) * mm, "end": v(45.24, 28.97) * mm});
            skLineSegment(sketch, "E237.MirrorCS", {"start": v(13.5, 30.96) * mm, "end": v(13.5, 28.58) * mm});
            skLineSegment(sketch, "E238.MirrorCS", {"start": v(50, 5.56) * mm, "end": v(48.02, 5.56) * mm});
            skPoint(sketch, "E239.MirrorP", {"position": v(2.38, 28.57) * mm});
            skLineSegment(sketch, "E240.MirrorCS", {"start": v(42.07, 30.96) * mm, "end": v(42.07, 28.97) * mm});
            skLineSegment(sketch, "E241.MirrorCS", {"start": v(46.83, 28.57) * mm, "end": v(46.83, 26.6) * mm});
            skLineSegment(sketch, "E242.MirrorCS", {"start": v(50, 7.14) * mm, "end": v(48.02, 7.14) * mm});
            skPoint(sketch, "E243.MirrorP", {"position": v(19.84, 28.58) * mm});
            skLineSegment(sketch, "E244.MirrorCS", {"start": v(30.96, 30.96) * mm, "end": v(30.96, 28.97) * mm});
            skPoint(sketch, "E245.MirrorP", {"position": v(26.2, 28.58) * mm});
            skLineSegment(sketch, "E246.MirrorCS", {"start": v(50, 21.43) * mm, "end": v(48.02, 21.43) * mm});
            skLineSegment(sketch, "E247.MirrorCS", {"start": v(38.9, 30.96) * mm, "end": v(38.9, 28.97) * mm});
            skLineSegment(sketch, "E248.MirrorCS", {"start": v(27.78, 30.96) * mm, "end": v(27.78, 28.97) * mm});
            skPoint(sketch, "E249.MirrorP", {"position": v(7.14, 28.57) * mm});
            skLineSegment(sketch, "E250.MirrorCS", {"start": v(0.8, 30.96) * mm, "end": v(0.8, 28.97) * mm});
            skLineSegment(sketch, "E251.MirrorCS", {"start": v(35.72, 30.96) * mm, "end": v(35.72, 28.97) * mm});
            skLineSegment(sketch, "E252.MirrorCS", {"start": v(40.48, 30.96) * mm, "end": v(40.48, 28.97) * mm});
            skLineSegment(sketch, "E253.MirrorCS", {"start": v(10.32, 30.96) * mm, "end": v(10.32, 28.97) * mm});
            skLineSegment(sketch, "E254.MirrorCS", {"start": v(50, 3.97) * mm, "end": v(48.02, 3.97) * mm});
            skPoint(sketch, "E255.MirrorP", {"position": v(46.83, 26.2) * mm});
            skPoint(sketch, "E256.MirrorP", {"position": v(5.56, 28.57) * mm});
            skPoint(sketch, "E257.MirrorP", {"position": v(47.62, 16.67) * mm});
            skPoint(sketch, "E258.MirrorP", {"position": v(47.62, 3.97) * mm});
            skPoint(sketch, "E259.MirrorP", {"position": v(35.72, 28.58) * mm});
            skPoint(sketch, "E260.MirrorP", {"position": v(47.62, 19.84) * mm});
            skPoint(sketch, "E261.MirrorP", {"position": v(38.9, 28.58) * mm});
            skLineSegment(sketch, "E262.MirrorCS", {"start": v(50, 11.9) * mm, "end": v(48.02, 11.9) * mm});
            skLineSegment(sketch, "E263.MirrorCS", {"start": v(8.73, 30.96) * mm, "end": v(8.73, 28.97) * mm});
            skLineSegment(sketch, "E264.MirrorCS", {"start": v(50, 13.5) * mm, "end": v(48.02, 13.5) * mm});
            skLineSegment(sketch, "E265.MirrorCS", {"start": v(18.26, 30.96) * mm, "end": v(18.26, 28.58) * mm});
            skLineSegment(sketch, "E266.MirrorCS", {"start": v(26.2, 30.96) * mm, "end": v(26.2, 28.97) * mm});
            skLineSegment(sketch, "E267.MirrorCS", {"start": v(50, 18.26) * mm, "end": v(48.02, 18.26) * mm});
            skPoint(sketch, "E268.MirrorP", {"position": v(47.62, 2.38) * mm});
            skPoint(sketch, "E269.MirrorP", {"position": v(47.62, 15.08) * mm});
            skPoint(sketch, "E270.MirrorP", {"position": v(37.3, 28.58) * mm});
            skCircle(sketch, "E271.MirrorC", {"center": v(15.88, 28.57) * mm, "radius": 1.2 * mm});
            skPoint(sketch, "E272.MirrorP", {"position": v(47.62, 0.8) * mm});
            skArc(sketch, "E273.MirrorCS", {"start": v(18.26, 28.58) * mm, "mid": v(15.88, 26.2) * mm, "end": v(13.5, 28.58) * mm});
            skCircle(sketch, "E274.MirrorC", {"center": v(49.21, 28.58) * mm, "radius": 1.2 * mm});
            skLineSegment(sketch, "E275.MirrorCS", {"start": v(47.62, -8.33) * mm, "end": v(47.62, -7.54) * mm});
            skLineSegment(sketch, "E276.MirrorCS", {"start": v(47.62, -5.16) * mm, "end": v(47.62, -4.37) * mm});
            skArc(sketch, "E277.MirrorCS", {"start": v(47.62, -8.33) * mm, "mid": v(47.74, -8.62) * mm, "end": v(48.02, -8.73) * mm});
            skArc(sketch, "E278.MirrorCS", {"start": v(47.62, -5.16) * mm, "mid": v(47.74, -5.44) * mm, "end": v(48.02, -5.56) * mm});
            skLineSegment(sketch, "E279.MirrorCS", {"start": v(-39.3, -28.58) * mm, "end": v(-40.08, -28.58) * mm});
            skArc(sketch, "E280.MirrorCS", {"start": v(-39.3, -28.58) * mm, "mid": v(-39, -28.7) * mm, "end": v(-38.9, -28.97) * mm});
            skArc(sketch, "E281.MirrorCS", {"start": v(-7.54, -28.57) * mm, "mid": v(-7.26, -28.7) * mm, "end": v(-7.14, -28.97) * mm});
            skArc(sketch, "E282.MirrorCS", {"start": v(-47.23, -26.2) * mm, "mid": v(-46.95, -26.3) * mm, "end": v(-46.83, -26.6) * mm});
            skArc(sketch, "E283.MirrorCS", {"start": v(1.2, -28.57) * mm, "mid": v(0.9, -28.7) * mm, "end": v(0.8, -28.97) * mm});
            skLineSegment(sketch, "E284.MirrorCS", {"start": v(-47.62, -14.68) * mm, "end": v(-47.62, -13.9) * mm});
            skLineSegment(sketch, "E285.MirrorCS", {"start": v(-36.12, -28.58) * mm, "end": v(-36.9, -28.58) * mm});
            skLineSegment(sketch, "E286.MirrorCS", {"start": v(47.62, -17.86) * mm, "end": v(47.62, -17.07) * mm});
            skArc(sketch, "E287.MirrorCS", {"start": v(48.02, -0.8) * mm, "mid": v(47.74, -0.9) * mm, "end": v(47.62, -1.2) * mm});
            skLineSegment(sketch, "E288.MirrorCS", {"start": v(-47.62, -11.5) * mm, "end": v(-47.62, -10.72) * mm});
            skArc(sketch, "E289.MirrorCS", {"start": v(-47.23, -26.2) * mm, "mid": v(-47.5, -26.08) * mm, "end": v(-47.62, -25.8) * mm});
            skArc(sketch, "E290.MirrorCS", {"start": v(-26.6, -28.58) * mm, "mid": v(-26.3, -28.7) * mm, "end": v(-26.2, -28.97) * mm});
            skLineSegment(sketch, "E291.MirrorCS", {"start": v(-47.62, -17.86) * mm, "end": v(-47.62, -17.07) * mm});
            skLineSegment(sketch, "E292.MirrorCS", {"start": v(47.62, -14.68) * mm, "end": v(47.62, -13.9) * mm});
            skLineSegment(sketch, "E293.MirrorCS", {"start": v(-7.54, -28.57) * mm, "end": v(-8.33, -28.57) * mm});
            skLineSegment(sketch, "E294.MirrorCS", {"start": v(-26.6, -28.58) * mm, "end": v(-27.38, -28.58) * mm});
            skArc(sketch, "E295.MirrorCS", {"start": v(-37.3, -28.97) * mm, "mid": v(-37.2, -28.7) * mm, "end": v(-36.9, -28.57) * mm});
            skLineSegment(sketch, "E296.MirrorCS", {"start": v(47.62, -21.03) * mm, "end": v(47.62, -20.24) * mm});
            skArc(sketch, "E297.MirrorCS", {"start": v(48.02, -3.97) * mm, "mid": v(47.74, -4.08) * mm, "end": v(47.62, -4.37) * mm});
            skLineSegment(sketch, "E298.MirrorCS", {"start": v(-47.62, -5.16) * mm, "end": v(-47.62, -4.37) * mm});
            skArc(sketch, "E299.MirrorCS", {"start": v(-27.78, -28.97) * mm, "mid": v(-27.67, -28.7) * mm, "end": v(-27.38, -28.57) * mm});
            skLineSegment(sketch, "E300.MirrorCS", {"start": v(47.62, -1.98) * mm, "end": v(47.62, -1.2) * mm});
            skLineSegment(sketch, "E301.MirrorCS", {"start": v(47.62, -11.5) * mm, "end": v(47.62, -10.72) * mm});
            skLineSegment(sketch, "E302.MirrorCS", {"start": v(1.2, -28.57) * mm, "end": v(1.98, -28.57) * mm});
            skArc(sketch, "E303.MirrorCS", {"start": v(-47.62, -11.5) * mm, "mid": v(-47.74, -11.8) * mm, "end": v(-48.02, -11.9) * mm});
            skArc(sketch, "E304.MirrorCS", {"start": v(-47.62, -17.86) * mm, "mid": v(-47.74, -18.14) * mm, "end": v(-48.02, -18.26) * mm});
            skArc(sketch, "E305.MirrorCS", {"start": v(48.02, -16.67) * mm, "mid": v(47.74, -16.78) * mm, "end": v(47.62, -17.07) * mm});
            skLineSegment(sketch, "E306.MirrorCS", {"start": v(-1.2, -28.57) * mm, "end": v(-1.98, -28.57) * mm});
            skArc(sketch, "E307.MirrorCS", {"start": v(47.62, -1.98) * mm, "mid": v(47.74, -2.27) * mm, "end": v(48.02, -2.38) * mm});
            skArc(sketch, "E308.MirrorCS", {"start": v(-2.38, -28.97) * mm, "mid": v(-2.27, -28.7) * mm, "end": v(-1.98, -28.57) * mm});
            skArc(sketch, "E309.MirrorCS", {"start": v(48.02, -13.5) * mm, "mid": v(47.74, -13.6) * mm, "end": v(47.62, -13.9) * mm});
            skArc(sketch, "E310.MirrorCS", {"start": v(-47.62, -14.68) * mm, "mid": v(-47.74, -14.97) * mm, "end": v(-48.02, -15.08) * mm});
            skArc(sketch, "E311.MirrorCS", {"start": v(47.62, -11.5) * mm, "mid": v(47.74, -11.8) * mm, "end": v(48.02, -11.9) * mm});
            skArc(sketch, "E312.MirrorCS", {"start": v(-40.48, -28.97) * mm, "mid": v(-40.37, -28.7) * mm, "end": v(-40.08, -28.58) * mm});
            skArc(sketch, "E313.MirrorCS", {"start": v(47.62, -14.68) * mm, "mid": v(47.74, -14.97) * mm, "end": v(48.02, -15.08) * mm});
            skArc(sketch, "E314.MirrorCS", {"start": v(48.02, -19.84) * mm, "mid": v(47.74, -19.96) * mm, "end": v(47.62, -20.24) * mm});
            skArc(sketch, "E315.MirrorCS", {"start": v(47.62, -17.86) * mm, "mid": v(47.74, -18.14) * mm, "end": v(48.02, -18.26) * mm});
            skArc(sketch, "E316.MirrorCS", {"start": v(-47.62, -5.16) * mm, "mid": v(-47.74, -5.44) * mm, "end": v(-48.02, -5.56) * mm});
            skArc(sketch, "E317.MirrorCS", {"start": v(48.02, -10.32) * mm, "mid": v(47.74, -10.43) * mm, "end": v(47.62, -10.72) * mm});
            skArc(sketch, "E318.MirrorCS", {"start": v(-48.02, -7.14) * mm, "mid": v(-47.74, -7.26) * mm, "end": v(-47.62, -7.54) * mm});
            skArc(sketch, "E319.MirrorCS", {"start": v(-10.72, -28.57) * mm, "mid": v(-10.43, -28.7) * mm, "end": v(-10.32, -28.97) * mm});
            skArc(sketch, "E320.MirrorCS", {"start": v(-48.02, -3.97) * mm, "mid": v(-47.74, -4.08) * mm, "end": v(-47.62, -4.37) * mm});
            skArc(sketch, "E321.MirrorCS", {"start": v(-47.62, -1.98) * mm, "mid": v(-47.74, -2.27) * mm, "end": v(-48.02, -2.38) * mm});
            skArc(sketch, "E322.MirrorCS", {"start": v(-20.24, -28.58) * mm, "mid": v(-19.96, -28.7) * mm, "end": v(-19.84, -28.97) * mm});
            skArc(sketch, "E323.MirrorCS", {"start": v(-21.43, -28.97) * mm, "mid": v(-21.32, -28.7) * mm, "end": v(-21.03, -28.58) * mm});
            skArc(sketch, "E324.MirrorCS", {"start": v(-34.13, -28.97) * mm, "mid": v(-34.02, -28.7) * mm, "end": v(-33.73, -28.58) * mm});
            skArc(sketch, "E325.MirrorCS", {"start": v(-48.02, -19.84) * mm, "mid": v(-47.74, -19.96) * mm, "end": v(-47.62, -20.24) * mm});
            skLineSegment(sketch, "E326.MirrorCS", {"start": v(-42.47, -28.58) * mm, "end": v(-43.26, -28.58) * mm});
            skLineSegment(sketch, "E327.MirrorCS", {"start": v(-47.62, -8.33) * mm, "end": v(-47.62, -7.54) * mm});
            skArc(sketch, "E328.MirrorCS", {"start": v(-36.12, -28.58) * mm, "mid": v(-35.83, -28.7) * mm, "end": v(-35.72, -28.97) * mm});
            skLineSegment(sketch, "E329.MirrorCS", {"start": v(4.37, -28.57) * mm, "end": v(5.16, -28.57) * mm});
            skLineSegment(sketch, "E330.MirrorCS", {"start": v(-47.62, -21.03) * mm, "end": v(-47.62, -20.24) * mm});
            skArc(sketch, "E331.MirrorCS", {"start": v(29.77, -28.58) * mm, "mid": v(29.48, -28.7) * mm, "end": v(29.37, -28.97) * mm});
            skArc(sketch, "E332.MirrorCS", {"start": v(-30.96, -28.97) * mm, "mid": v(-30.84, -28.7) * mm, "end": v(-30.56, -28.58) * mm});
            skArc(sketch, "E333.MirrorCS", {"start": v(-29.77, -28.58) * mm, "mid": v(-29.48, -28.7) * mm, "end": v(-29.37, -28.97) * mm});
            skArc(sketch, "E334.MirrorCS", {"start": v(42.47, -28.58) * mm, "mid": v(42.18, -28.7) * mm, "end": v(42.07, -28.97) * mm});
            skLineSegment(sketch, "E335.MirrorCS", {"start": v(-20.24, -28.58) * mm, "end": v(-21.03, -28.58) * mm});
            skArc(sketch, "E336.MirrorCS", {"start": v(-47.62, -21.03) * mm, "mid": v(-47.74, -21.32) * mm, "end": v(-48.02, -21.43) * mm});
            skLineSegment(sketch, "E337.MirrorCS", {"start": v(-4.37, -28.57) * mm, "end": v(-5.16, -28.57) * mm});
            skArc(sketch, "E338.MirrorCS", {"start": v(-8.73, -28.97) * mm, "mid": v(-8.62, -28.7) * mm, "end": v(-8.33, -28.57) * mm});
            skLineSegment(sketch, "E339.MirrorCS", {"start": v(10.72, -28.57) * mm, "end": v(11.5, -28.57) * mm});
            skArc(sketch, "E340.MirrorCS", {"start": v(-48.02, -0.8) * mm, "mid": v(-47.74, -0.9) * mm, "end": v(-47.62, -1.2) * mm});
            skArc(sketch, "E341.MirrorCS", {"start": v(-1.2, -28.57) * mm, "mid": v(-0.9, -28.7) * mm, "end": v(-0.8, -28.97) * mm});
            skLineSegment(sketch, "E342.MirrorCS", {"start": v(39.3, -28.58) * mm, "end": v(40.08, -28.58) * mm});
            skArc(sketch, "E343.MirrorCS", {"start": v(39.3, -28.58) * mm, "mid": v(39, -28.7) * mm, "end": v(38.9, -28.97) * mm});
            skArc(sketch, "E344.MirrorCS", {"start": v(-11.9, -28.97) * mm, "mid": v(-11.8, -28.7) * mm, "end": v(-11.5, -28.57) * mm});
            skArc(sketch, "E345.MirrorCS", {"start": v(-23.42, -28.58) * mm, "mid": v(-23.13, -28.7) * mm, "end": v(-23.02, -28.97) * mm});
            skArc(sketch, "E346.MirrorCS", {"start": v(-4.37, -28.57) * mm, "mid": v(-4.08, -28.7) * mm, "end": v(-3.97, -28.97) * mm});
            skLineSegment(sketch, "E347.MirrorCS", {"start": v(-47.62, -1.98) * mm, "end": v(-47.62, -1.2) * mm});
            skLineSegment(sketch, "E348.MirrorCS", {"start": v(29.77, -28.58) * mm, "end": v(30.56, -28.58) * mm});
            skLineSegment(sketch, "E349.MirrorCS", {"start": v(-32.94, -28.58) * mm, "end": v(-33.73, -28.58) * mm});
            skArc(sketch, "E350.MirrorCS", {"start": v(-43.66, -28.97) * mm, "mid": v(-43.54, -28.7) * mm, "end": v(-43.26, -28.58) * mm});
            skArc(sketch, "E351.MirrorCS", {"start": v(-48.02, -16.67) * mm, "mid": v(-47.74, -16.78) * mm, "end": v(-47.62, -17.07) * mm});
            skArc(sketch, "E352.MirrorCS", {"start": v(34.13, -28.97) * mm, "mid": v(34.02, -28.7) * mm, "end": v(33.73, -28.58) * mm});
            skArc(sketch, "E353.MirrorCS", {"start": v(27.78, -28.97) * mm, "mid": v(27.67, -28.7) * mm, "end": v(27.38, -28.57) * mm});
            skArc(sketch, "E354.MirrorCS", {"start": v(2.38, -28.97) * mm, "mid": v(2.27, -28.7) * mm, "end": v(1.98, -28.57) * mm});
            skArc(sketch, "E355.MirrorCS", {"start": v(-5.56, -28.97) * mm, "mid": v(-5.44, -28.7) * mm, "end": v(-5.16, -28.57) * mm});
            skLineSegment(sketch, "E356.MirrorCS", {"start": v(32.94, -28.58) * mm, "end": v(33.73, -28.58) * mm});
            skArc(sketch, "E357.MirrorCS", {"start": v(23.42, -28.58) * mm, "mid": v(23.13, -28.7) * mm, "end": v(23.02, -28.97) * mm});
            skArc(sketch, "E358.MirrorCS", {"start": v(-42.47, -28.58) * mm, "mid": v(-42.18, -28.7) * mm, "end": v(-42.07, -28.97) * mm});
            skArc(sketch, "E359.MirrorCS", {"start": v(-48.02, -10.32) * mm, "mid": v(-47.74, -10.43) * mm, "end": v(-47.62, -10.72) * mm});
            skArc(sketch, "E360.MirrorCS", {"start": v(-24.6, -28.97) * mm, "mid": v(-24.5, -28.7) * mm, "end": v(-24.2, -28.58) * mm});
            skArc(sketch, "E361.MirrorCS", {"start": v(-47.62, -8.33) * mm, "mid": v(-47.74, -8.62) * mm, "end": v(-48.02, -8.73) * mm});
            skLineSegment(sketch, "E362.MirrorCS", {"start": v(0, -30.96) * mm, "end": v(-0.8, -30.96) * mm});
            skArc(sketch, "E363.MirrorCS", {"start": v(32.94, -28.58) * mm, "mid": v(32.66, -28.7) * mm, "end": v(32.54, -28.97) * mm});
            skArc(sketch, "E364.MirrorCS", {"start": v(-32.94, -28.58) * mm, "mid": v(-32.66, -28.7) * mm, "end": v(-32.54, -28.97) * mm});
            skLineSegment(sketch, "E365.MirrorCS", {"start": v(42.47, -28.58) * mm, "end": v(43.26, -28.58) * mm});
            skLineSegment(sketch, "E366.MirrorCS", {"start": v(26.6, -28.58) * mm, "end": v(27.38, -28.58) * mm});
            skLineSegment(sketch, "E367.MirrorCS", {"start": v(-29.77, -28.58) * mm, "end": v(-30.56, -28.58) * mm});
            skArc(sketch, "E368.MirrorCS", {"start": v(10.72, -28.57) * mm, "mid": v(10.43, -28.7) * mm, "end": v(10.32, -28.97) * mm});
            skLineSegment(sketch, "E369.MirrorCS", {"start": v(-0.8, -30.96) * mm, "end": v(-0.8, -28.97) * mm});
            skLineSegment(sketch, "E370.MirrorCS", {"start": v(-23.42, -28.58) * mm, "end": v(-24.2, -28.58) * mm});
            skArc(sketch, "E371.MirrorCS", {"start": v(47.62, -21.03) * mm, "mid": v(47.74, -21.32) * mm, "end": v(48.02, -21.43) * mm});
            skArc(sketch, "E372.MirrorCS", {"start": v(4.37, -28.57) * mm, "mid": v(4.08, -28.7) * mm, "end": v(3.97, -28.97) * mm});
            skLineSegment(sketch, "E373.MirrorCS", {"start": v(-10.72, -28.57) * mm, "end": v(-11.5, -28.57) * mm});
            skLineSegment(sketch, "E374.MirrorCS", {"start": v(20.24, -28.58) * mm, "end": v(21.03, -28.58) * mm});
            skLineSegment(sketch, "E375.MirrorCS", {"start": v(-50, -8.73) * mm, "end": v(-48.02, -8.73) * mm});
            skLineSegment(sketch, "E376.MirrorCS", {"start": v(-40.48, -30.96) * mm, "end": v(-42.07, -30.96) * mm});
            skLineSegment(sketch, "E377.MirrorCS", {"start": v(-50, -10.32) * mm, "end": v(-50, -8.73) * mm});
            skLineSegment(sketch, "E378.MirrorCS", {"start": v(-34.13, -30.96) * mm, "end": v(-34.13, -28.97) * mm});
            skLineSegment(sketch, "E379.MirrorCS", {"start": v(-27.78, -30.96) * mm, "end": v(-27.78, -28.97) * mm});
            skLineSegment(sketch, "E380.MirrorCS", {"start": v(-34.13, -30.96) * mm, "end": v(-35.72, -30.96) * mm});
            skArc(sketch, "E381.MirrorCS", {"start": v(20.24, -28.58) * mm, "mid": v(19.96, -28.7) * mm, "end": v(19.84, -28.97) * mm});
            skArc(sketch, "E382.MirrorCS", {"start": v(8.73, -28.97) * mm, "mid": v(8.62, -28.7) * mm, "end": v(8.33, -28.57) * mm});
            skArc(sketch, "E383.MirrorCS", {"start": v(7.54, -28.57) * mm, "mid": v(7.26, -28.7) * mm, "end": v(7.14, -28.97) * mm});
            skLineSegment(sketch, "E384.MirrorCS", {"start": v(36.12, -28.58) * mm, "end": v(36.9, -28.58) * mm});
            skLineSegment(sketch, "E385.MirrorCS", {"start": v(-47.62, -23.42) * mm, "end": v(-47.62, -25.8) * mm});
            skArc(sketch, "E386.MirrorCS", {"start": v(5.56, -28.97) * mm, "mid": v(5.44, -28.7) * mm, "end": v(5.16, -28.57) * mm});
            skLineSegment(sketch, "E387.MirrorCS", {"start": v(-50, -23.02) * mm, "end": v(-48.02, -23.02) * mm});
            skLineSegment(sketch, "E388.MirrorCS", {"start": v(-50, -21.43) * mm, "end": v(-48.02, -21.43) * mm});
            skLineSegment(sketch, "E389.MirrorCS", {"start": v(-38.9, -30.96) * mm, "end": v(-38.9, -28.97) * mm});
            skArc(sketch, "E390.MirrorCS", {"start": v(-45.64, -28.58) * mm, "mid": v(-45.36, -28.7) * mm, "end": v(-45.24, -28.97) * mm});
            skLineSegment(sketch, "E391.MirrorCS", {"start": v(-26.2, -30.96) * mm, "end": v(-26.2, -28.97) * mm});
            skLineSegment(sketch, "E392.MirrorCS", {"start": v(-18.26, -30.96) * mm, "end": v(-18.26, -28.58) * mm});
            skLineSegment(sketch, "E393.MirrorCS", {"start": v(0, -30.96) * mm, "end": v(0.8, -30.96) * mm});
            skLineSegment(sketch, "E394.MirrorCS", {"start": v(-19.84, -30.96) * mm, "end": v(-19.84, -28.97) * mm});
            skLineSegment(sketch, "E395.MirrorCS", {"start": v(-50, -5.56) * mm, "end": v(-48.02, -5.56) * mm});
            skLineSegment(sketch, "E396.MirrorCS", {"start": v(-13.5, -30.96) * mm, "end": v(-13.5, -28.58) * mm});
            skLineSegment(sketch, "E397.MirrorCS", {"start": v(-50, -10.32) * mm, "end": v(-48.02, -10.32) * mm});
            skLineSegment(sketch, "E398.MirrorCS", {"start": v(-43.66, -30.96) * mm, "end": v(-45.24, -30.96) * mm});
            skLineSegment(sketch, "E399.MirrorCS", {"start": v(-50, -23.02) * mm, "end": v(-50, -21.43) * mm});
            skLineSegment(sketch, "E400.MirrorCS", {"start": v(-35.72, -30.96) * mm, "end": v(-35.72, -28.97) * mm});
            skLineSegment(sketch, "E401.MirrorCS", {"start": v(-45.64, -28.57) * mm, "end": v(-46.83, -28.57) * mm});
            skLineSegment(sketch, "E402.MirrorCS", {"start": v(-11.9, -30.96) * mm, "end": v(-13.5, -30.96) * mm});
            skArc(sketch, "E403.MirrorCS", {"start": v(37.3, -28.97) * mm, "mid": v(37.2, -28.7) * mm, "end": v(36.9, -28.57) * mm});
            skLineSegment(sketch, "E404.MirrorCS", {"start": v(-50, -18.26) * mm, "end": v(-48.02, -18.26) * mm});
            skLineSegment(sketch, "E405.MirrorCS", {"start": v(-50, -19.84) * mm, "end": v(-48.02, -19.84) * mm});
            skArc(sketch, "E406.MirrorCS", {"start": v(45.64, -28.58) * mm, "mid": v(45.36, -28.7) * mm, "end": v(45.24, -28.97) * mm});
            skArc(sketch, "E407.MirrorCS", {"start": v(21.43, -28.97) * mm, "mid": v(21.32, -28.7) * mm, "end": v(21.03, -28.58) * mm});
            skLineSegment(sketch, "E408.MirrorCS", {"start": v(-46.83, -28.57) * mm, "end": v(-46.83, -26.6) * mm});
            skLineSegment(sketch, "E409.MirrorCS", {"start": v(-50, -7.14) * mm, "end": v(-48.02, -7.14) * mm});
            skLineSegment(sketch, "E410.MirrorCS", {"start": v(-50, -19.84) * mm, "end": v(-50, -18.26) * mm});
            skLineSegment(sketch, "E411.MirrorCS", {"start": v(-50, -16.67) * mm, "end": v(-48.02, -16.67) * mm});
            skLineSegment(sketch, "E412.MirrorCS", {"start": v(-50, -15.08) * mm, "end": v(-48.02, -15.08) * mm});
            skLineSegment(sketch, "E413.MirrorCS", {"start": v(-18.26, -30.96) * mm, "end": v(-19.84, -30.96) * mm});
            skArc(sketch, "E414.MirrorCS", {"start": v(48.02, -23.02) * mm, "mid": v(47.74, -23.13) * mm, "end": v(47.62, -23.42) * mm});
            skArc(sketch, "E415.MirrorCS", {"start": v(36.12, -28.58) * mm, "mid": v(35.83, -28.7) * mm, "end": v(35.72, -28.97) * mm});
            skLineSegment(sketch, "E416.MirrorCS", {"start": v(-11.9, -30.96) * mm, "end": v(-11.9, -28.97) * mm});
            skLineSegment(sketch, "E417.MirrorCS", {"start": v(-32.54, -30.96) * mm, "end": v(-32.54, -28.97) * mm});
            skLineSegment(sketch, "E418.MirrorCS", {"start": v(-50, -16.67) * mm, "end": v(-50, -15.08) * mm});
            skLineSegment(sketch, "E419.MirrorCS", {"start": v(7.54, -28.57) * mm, "end": v(8.33, -28.57) * mm});
            skArc(sketch, "E420.MirrorCS", {"start": v(-48.02, -13.5) * mm, "mid": v(-47.74, -13.6) * mm, "end": v(-47.62, -13.9) * mm});
            skLineSegment(sketch, "E421.MirrorCS", {"start": v(-50, -2.38) * mm, "end": v(-48.02, -2.38) * mm});
            skLineSegment(sketch, "E422.MirrorCS", {"start": v(-2.38, -30.96) * mm, "end": v(-2.38, -28.97) * mm});
            skLineSegment(sketch, "E423.MirrorCS", {"start": v(-23.02, -30.96) * mm, "end": v(-23.02, -28.97) * mm});
            skLineSegment(sketch, "E424.MirrorCS", {"start": v(0.8, -30.96) * mm, "end": v(0.8, -28.97) * mm});
            skLineSegment(sketch, "E425.MirrorCS", {"start": v(-50, -13.5) * mm, "end": v(-48.02, -13.5) * mm});
            skLineSegment(sketch, "E426.MirrorCS", {"start": v(-37.3, -30.96) * mm, "end": v(-38.9, -30.96) * mm});
            skLineSegment(sketch, "E427.MirrorCS", {"start": v(-30.96, -30.96) * mm, "end": v(-30.96, -28.97) * mm});
            skLineSegment(sketch, "E428.MirrorCS", {"start": v(-50, -0.8) * mm, "end": v(-48.02, -0.8) * mm});
            skLineSegment(sketch, "E429.MirrorCS", {"start": v(-50, -3.97) * mm, "end": v(-48.02, -3.97) * mm});
            skLineSegment(sketch, "E430.MirrorCS", {"start": v(-10.32, -30.96) * mm, "end": v(-10.32, -28.97) * mm});
            skLineSegment(sketch, "E431.MirrorCS", {"start": v(-24.6, -30.96) * mm, "end": v(-24.6, -28.97) * mm});
            skLineSegment(sketch, "E432.MirrorCS", {"start": v(-30.96, -30.96) * mm, "end": v(-32.54, -30.96) * mm});
            skLineSegment(sketch, "E433.MirrorCS", {"start": v(-50, -7.14) * mm, "end": v(-50, -5.56) * mm});
            skArc(sketch, "E434.MirrorCS", {"start": v(30.96, -28.97) * mm, "mid": v(30.84, -28.7) * mm, "end": v(30.56, -28.58) * mm});
            skArc(sketch, "E435.MirrorCS", {"start": v(24.6, -28.97) * mm, "mid": v(24.5, -28.7) * mm, "end": v(24.2, -28.58) * mm});
            skLineSegment(sketch, "E436.MirrorCS", {"start": v(-50, -11.9) * mm, "end": v(-48.02, -11.9) * mm});
            skLineSegment(sketch, "E437.MirrorCS", {"start": v(-29.37, -30.96) * mm, "end": v(-29.37, -28.97) * mm});
            skLineSegment(sketch, "E438.MirrorCS", {"start": v(-50, -0.8) * mm, "end": v(-50, 0) * mm});
            skLineSegment(sketch, "E439.MirrorCS", {"start": v(23.42, -28.58) * mm, "end": v(24.2, -28.58) * mm});
            skLineSegment(sketch, "E440.MirrorCS", {"start": v(-50, -13.5) * mm, "end": v(-50, -11.9) * mm});
            skLineSegment(sketch, "E441.MirrorCS", {"start": v(-27.78, -30.96) * mm, "end": v(-29.37, -30.96) * mm});
            skLineSegment(sketch, "E442.MirrorCS", {"start": v(-43.66, -30.96) * mm, "end": v(-43.66, -28.97) * mm});
            skLineSegment(sketch, "E443.MirrorCS", {"start": v(-21.43, -30.96) * mm, "end": v(-21.43, -28.97) * mm});
            skArc(sketch, "E444.MirrorCS", {"start": v(48.02, -7.14) * mm, "mid": v(47.74, -7.26) * mm, "end": v(47.62, -7.54) * mm});
            skArc(sketch, "E445.MirrorCS", {"start": v(26.6, -28.58) * mm, "mid": v(26.3, -28.7) * mm, "end": v(26.2, -28.97) * mm});
            skLineSegment(sketch, "E446.MirrorCS", {"start": v(-40.48, -30.96) * mm, "end": v(-40.48, -28.97) * mm});
            skLineSegment(sketch, "E447.MirrorCS", {"start": v(-50, -3.97) * mm, "end": v(-50, -2.38) * mm});
            skLineSegment(sketch, "E448.MirrorCS", {"start": v(-45.24, -30.96) * mm, "end": v(-45.24, -28.97) * mm});
            skLineSegment(sketch, "E449.MirrorCS", {"start": v(-24.6, -30.96) * mm, "end": v(-26.2, -30.96) * mm});
            skLineSegment(sketch, "E450.MirrorCS", {"start": v(-21.43, -30.96) * mm, "end": v(-23.02, -30.96) * mm});
            skLineSegment(sketch, "E451.MirrorCS", {"start": v(-37.3, -30.96) * mm, "end": v(-37.3, -28.97) * mm});
            skLineSegment(sketch, "E452.MirrorCS", {"start": v(-42.07, -30.96) * mm, "end": v(-42.07, -28.97) * mm});
            skArc(sketch, "E453.MirrorCS", {"start": v(-48.02, -23.02) * mm, "mid": v(-47.74, -23.13) * mm, "end": v(-47.62, -23.42) * mm});
            skLineSegment(sketch, "E454.MirrorCS", {"start": v(50, -2.38) * mm, "end": v(48.02, -2.38) * mm});
            skLineSegment(sketch, "E455.MirrorCS", {"start": v(30.96, -30.96) * mm, "end": v(30.96, -28.97) * mm});
            skLineSegment(sketch, "E456.MirrorCS", {"start": v(43.66, -30.96) * mm, "end": v(43.66, -28.97) * mm});
            skLineSegment(sketch, "E457.MirrorCS", {"start": v(-5.56, -30.96) * mm, "end": v(-5.56, -28.97) * mm});
            skArc(sketch, "E458.MirrorCS", {"start": v(47.23, -26.2) * mm, "mid": v(46.95, -26.3) * mm, "end": v(46.83, -26.6) * mm});
            skLineSegment(sketch, "E459.MirrorCS", {"start": v(50, -13.5) * mm, "end": v(48.02, -13.5) * mm});
            skArc(sketch, "E460.MirrorCS", {"start": v(40.48, -28.97) * mm, "mid": v(40.37, -28.7) * mm, "end": v(40.08, -28.58) * mm});
            skLineSegment(sketch, "E461.MirrorCS", {"start": v(50, -3.97) * mm, "end": v(50, -2.38) * mm});
            skLineSegment(sketch, "E462.MirrorCS", {"start": v(24.6, -30.96) * mm, "end": v(26.2, -30.96) * mm});
            skLineSegment(sketch, "E463.MirrorCS", {"start": v(50, -16.67) * mm, "end": v(50, -15.08) * mm});
            skLineSegment(sketch, "E464.MirrorCS", {"start": v(37.3, -30.96) * mm, "end": v(38.9, -30.96) * mm});
            skLineSegment(sketch, "E465.MirrorCS", {"start": v(30.96, -30.96) * mm, "end": v(32.54, -30.96) * mm});
            skPoint(sketch, "E466.MirrorP", {"position": v(-35.72, -28.58) * mm});
            skLineSegment(sketch, "E467.MirrorCS", {"start": v(34.13, -30.96) * mm, "end": v(35.72, -30.96) * mm});
            skLineSegment(sketch, "E468.MirrorCS", {"start": v(50, -18.26) * mm, "end": v(48.02, -18.26) * mm});
            skArc(sketch, "E469.MirrorCS", {"start": v(11.9, -28.97) * mm, "mid": v(11.8, -28.7) * mm, "end": v(11.5, -28.57) * mm});
            skArc(sketch, "E470.MirrorCS", {"start": v(47.23, -26.2) * mm, "mid": v(47.5, -26.08) * mm, "end": v(47.62, -25.8) * mm});
            skPoint(sketch, "E471.MirrorP", {"position": v(-8.73, -28.57) * mm});
            skLineSegment(sketch, "E472.MirrorCS", {"start": v(-2.38, -30.96) * mm, "end": v(-3.97, -30.96) * mm});
            skLineSegment(sketch, "E473.MirrorCS", {"start": v(8.73, -30.96) * mm, "end": v(8.73, -28.97) * mm});
            skLineSegment(sketch, "E474.MirrorCS", {"start": v(50, -0.8) * mm, "end": v(50, 0) * mm});
            skLineSegment(sketch, "E475.MirrorCS", {"start": v(13.5, -30.96) * mm, "end": v(13.5, -28.58) * mm});
            skLineSegment(sketch, "E476.MirrorCS", {"start": v(50, -23.02) * mm, "end": v(50, -21.43) * mm});
            skPoint(sketch, "E477.MirrorP", {"position": v(-3.97, -28.57) * mm});
            skLineSegment(sketch, "E478.MirrorCS", {"start": v(26.2, -30.96) * mm, "end": v(26.2, -28.97) * mm});
            skLineSegment(sketch, "E479.MirrorCS", {"start": v(42.07, -30.96) * mm, "end": v(42.07, -28.97) * mm});
            skLineSegment(sketch, "E480.MirrorCS", {"start": v(50, -21.43) * mm, "end": v(48.02, -21.43) * mm});
            skLineSegment(sketch, "E481.MirrorCS", {"start": v(34.13, -30.96) * mm, "end": v(34.13, -28.97) * mm});
            skLineSegment(sketch, "E482.MirrorCS", {"start": v(29.37, -30.96) * mm, "end": v(29.37, -28.97) * mm});
            skLineSegment(sketch, "E483.MirrorCS", {"start": v(46.83, -28.57) * mm, "end": v(46.83, -26.6) * mm});
            skLineSegment(sketch, "E484.MirrorCS", {"start": v(21.43, -30.96) * mm, "end": v(21.43, -28.97) * mm});
            skLineSegment(sketch, "E485.MirrorCS", {"start": v(-3.97, -30.96) * mm, "end": v(-3.97, -28.97) * mm});
            skLineSegment(sketch, "E486.MirrorCS", {"start": v(50, -10.32) * mm, "end": v(50, -8.73) * mm});
            skLineSegment(sketch, "E487.MirrorCS", {"start": v(50, -7.14) * mm, "end": v(48.02, -7.14) * mm});
            skLineSegment(sketch, "E488.MirrorCS", {"start": v(45.24, -30.96) * mm, "end": v(45.24, -28.97) * mm});
            skLineSegment(sketch, "E489.MirrorCS", {"start": v(2.38, -30.96) * mm, "end": v(2.38, -28.97) * mm});
            skLineSegment(sketch, "E490.MirrorCS", {"start": v(50, -13.5) * mm, "end": v(50, -11.9) * mm});
            skPoint(sketch, "E491.MirrorP", {"position": v(-27.78, -28.58) * mm});
            skLineSegment(sketch, "E492.MirrorCS", {"start": v(21.43, -30.96) * mm, "end": v(23.02, -30.96) * mm});
            skLineSegment(sketch, "E493.MirrorCS", {"start": v(11.9, -30.96) * mm, "end": v(13.5, -30.96) * mm});
            skLineSegment(sketch, "E494.MirrorCS", {"start": v(18.26, -30.96) * mm, "end": v(18.26, -28.58) * mm});
            skLineSegment(sketch, "E495.MirrorCS", {"start": v(50, -5.56) * mm, "end": v(48.02, -5.56) * mm});
            skLineSegment(sketch, "E496.MirrorCS", {"start": v(19.84, -30.96) * mm, "end": v(19.84, -28.97) * mm});
            skLineSegment(sketch, "E497.MirrorCS", {"start": v(10.32, -30.96) * mm, "end": v(10.32, -28.97) * mm});
            skLineSegment(sketch, "E498.MirrorCS", {"start": v(50, -10.32) * mm, "end": v(48.02, -10.32) * mm});
            skLineSegment(sketch, "E499.MirrorCS", {"start": v(50, -8.73) * mm, "end": v(48.02, -8.73) * mm});
            skArc(sketch, "E500.MirrorCS", {"start": v(43.66, -28.97) * mm, "mid": v(43.54, -28.7) * mm, "end": v(43.26, -28.58) * mm});
            skLineSegment(sketch, "E501.MirrorCS", {"start": v(38.9, -30.96) * mm, "end": v(38.9, -28.97) * mm});
            skLineSegment(sketch, "E502.MirrorCS", {"start": v(50, -0.8) * mm, "end": v(48.02, -0.8) * mm});
            skLineSegment(sketch, "E503.MirrorCS", {"start": v(50, -19.84) * mm, "end": v(50, -18.26) * mm});
            skLineSegment(sketch, "E504.MirrorCS", {"start": v(18.26, -30.96) * mm, "end": v(19.84, -30.96) * mm});
            skLineSegment(sketch, "E505.MirrorCS", {"start": v(-8.73, -30.96) * mm, "end": v(-10.32, -30.96) * mm});
            skLineSegment(sketch, "E506.MirrorCS", {"start": v(2.38, -30.96) * mm, "end": v(3.97, -30.96) * mm});
            skPoint(sketch, "E507.MirrorP", {"position": v(-45.24, -28.57) * mm});
            skLineSegment(sketch, "E508.MirrorCS", {"start": v(5.56, -30.96) * mm, "end": v(5.56, -28.97) * mm});
            skLineSegment(sketch, "E509.MirrorCS", {"start": v(3.97, -30.96) * mm, "end": v(3.97, -28.97) * mm});
            skLineSegment(sketch, "E510.MirrorCS", {"start": v(27.78, -30.96) * mm, "end": v(27.78, -28.97) * mm});
            skLineSegment(sketch, "E511.MirrorCS", {"start": v(50, -7.14) * mm, "end": v(50, -5.56) * mm});
            skLineSegment(sketch, "E512.MirrorCS", {"start": v(50, -3.97) * mm, "end": v(48.02, -3.97) * mm});
            skLineSegment(sketch, "E513.MirrorCS", {"start": v(32.54, -30.96) * mm, "end": v(32.54, -28.97) * mm});
            skLineSegment(sketch, "E514.MirrorCS", {"start": v(24.6, -30.96) * mm, "end": v(24.6, -28.97) * mm});
            skLineSegment(sketch, "E515.MirrorCS", {"start": v(-8.73, -30.96) * mm, "end": v(-8.73, -28.97) * mm});
            skLineSegment(sketch, "E516.MirrorCS", {"start": v(50, -11.9) * mm, "end": v(48.02, -11.9) * mm});
            skLineSegment(sketch, "E517.MirrorCS", {"start": v(11.9, -30.96) * mm, "end": v(11.9, -28.97) * mm});
            skLineSegment(sketch, "E518.MirrorCS", {"start": v(23.02, -30.96) * mm, "end": v(23.02, -28.97) * mm});
            skLineSegment(sketch, "E519.MirrorCS", {"start": v(-7.14, -30.96) * mm, "end": v(-7.14, -28.97) * mm});
            skLineSegment(sketch, "E520.MirrorCS", {"start": v(40.48, -30.96) * mm, "end": v(42.07, -30.96) * mm});
            skLineSegment(sketch, "E521.MirrorCS", {"start": v(47.62, -23.42) * mm, "end": v(47.62, -25.8) * mm});
            skLineSegment(sketch, "E522.MirrorCS", {"start": v(50, -19.84) * mm, "end": v(48.02, -19.84) * mm});
            skLineSegment(sketch, "E523.MirrorCS", {"start": v(43.66, -30.96) * mm, "end": v(45.24, -30.96) * mm});
            skLineSegment(sketch, "E524.MirrorCS", {"start": v(50, -23.02) * mm, "end": v(48.02, -23.02) * mm});
            skLineSegment(sketch, "E525.MirrorCS", {"start": v(37.3, -30.96) * mm, "end": v(37.3, -28.97) * mm});
            skPoint(sketch, "E526.MirrorP", {"position": v(-38.9, -28.58) * mm});
            skLineSegment(sketch, "E527.MirrorCS", {"start": v(40.48, -30.96) * mm, "end": v(40.48, -28.97) * mm});
            skLineSegment(sketch, "E528.MirrorCS", {"start": v(27.78, -30.96) * mm, "end": v(29.37, -30.96) * mm});
            skLineSegment(sketch, "E529.MirrorCS", {"start": v(-5.56, -30.96) * mm, "end": v(-7.14, -30.96) * mm});
            skLineSegment(sketch, "E530.MirrorCS", {"start": v(45.64, -28.57) * mm, "end": v(46.83, -28.57) * mm});
            skPoint(sketch, "E531.MirrorP", {"position": v(-47.62, -7.14) * mm});
            skLineSegment(sketch, "E532.MirrorCS", {"start": v(7.14, -30.96) * mm, "end": v(7.14, -28.97) * mm});
            skPoint(sketch, "E533.MirrorP", {"position": v(-47.62, -19.84) * mm});
            skLineSegment(sketch, "E534.MirrorCS", {"start": v(35.72, -30.96) * mm, "end": v(35.72, -28.97) * mm});
            skLineSegment(sketch, "E535.MirrorCS", {"start": v(5.56, -30.96) * mm, "end": v(7.14, -30.96) * mm});
            skLineSegment(sketch, "E536.MirrorCS", {"start": v(50, -15.08) * mm, "end": v(48.02, -15.08) * mm});
            skLineSegment(sketch, "E537.MirrorCS", {"start": v(8.73, -30.96) * mm, "end": v(10.32, -30.96) * mm});
            skLineSegment(sketch, "E538.MirrorCS", {"start": v(50, -16.67) * mm, "end": v(48.02, -16.67) * mm});
            skPoint(sketch, "E539.MirrorP", {"position": v(-47.62, -15.08) * mm});
            skPoint(sketch, "E540.MirrorP", {"position": v(-47.62, -5.56) * mm});
            skPoint(sketch, "E541.MirrorP", {"position": v(-0.8, -28.57) * mm});
            skPoint(sketch, "E542.MirrorP", {"position": v(-19.84, -28.58) * mm});
            skCircle(sketch, "E543.MirrorC", {"center": v(-49.21, -28.58) * mm, "radius": 1.2 * mm});
            skPoint(sketch, "E544.MirrorP", {"position": v(-47.62, -18.26) * mm});
            skPoint(sketch, "E545.MirrorP", {"position": v(-23.02, -28.58) * mm});
            skPoint(sketch, "E546.MirrorP", {"position": v(2.38, -28.57) * mm});
            skPoint(sketch, "E547.MirrorP", {"position": v(-47.62, -3.97) * mm});
            skPoint(sketch, "E548.MirrorP", {"position": v(-47.62, -16.67) * mm});
            skPoint(sketch, "E549.MirrorP", {"position": v(34.13, -28.58) * mm});
            skArc(sketch, "E550.MirrorCS", {"start": v(-18.26, -28.58) * mm, "mid": v(-15.88, -26.2) * mm, "end": v(-13.5, -28.58) * mm});
            skPoint(sketch, "E551.MirrorP", {"position": v(-5.56, -28.57) * mm});
            skPoint(sketch, "E552.MirrorP", {"position": v(37.3, -28.58) * mm});
            skPoint(sketch, "E553.MirrorP", {"position": v(47.62, -5.56) * mm});
            skCircle(sketch, "E554.MirrorC", {"center": v(-15.88, -28.57) * mm, "radius": 1.2 * mm});
            skPoint(sketch, "E555.MirrorP", {"position": v(-37.3, -28.58) * mm});
            skPoint(sketch, "E556.MirrorP", {"position": v(-47.62, -2.38) * mm});
            skPoint(sketch, "E557.MirrorP", {"position": v(-46.83, -26.2) * mm});
            skPoint(sketch, "E558.MirrorP", {"position": v(-40.48, -28.58) * mm});
            skPoint(sketch, "E559.MirrorP", {"position": v(42.07, -28.57) * mm});
            skPoint(sketch, "E560.MirrorP", {"position": v(7.14, -28.57) * mm});
            skPoint(sketch, "E561.MirrorP", {"position": v(47.62, -18.26) * mm});
            skPoint(sketch, "E562.MirrorP", {"position": v(-32.54, -28.58) * mm});
            skPoint(sketch, "E563.MirrorP", {"position": v(-47.62, -13.5) * mm});
            skPoint(sketch, "E564.MirrorP", {"position": v(-2.38, -28.57) * mm});
            skPoint(sketch, "E565.MirrorP", {"position": v(-47.62, -10.32) * mm});
            skPoint(sketch, "E566.MirrorP", {"position": v(-47.62, -23.02) * mm});
            skPoint(sketch, "E567.MirrorP", {"position": v(-47.62, -11.9) * mm});
            skPoint(sketch, "E568.MirrorP", {"position": v(-10.32, -28.57) * mm});
            skPoint(sketch, "E569.MirrorP", {"position": v(-34.13, -28.58) * mm});
            skPoint(sketch, "E570.MirrorP", {"position": v(-43.66, -28.58) * mm});
            skPoint(sketch, "E571.MirrorP", {"position": v(-47.62, -8.73) * mm});
            skPoint(sketch, "E572.MirrorP", {"position": v(-47.62, -21.43) * mm});
            skPoint(sketch, "E573.MirrorP", {"position": v(-24.6, -28.58) * mm});
            skPoint(sketch, "E574.MirrorP", {"position": v(-26.2, -28.58) * mm});
            skPoint(sketch, "E575.MirrorP", {"position": v(-7.14, -28.57) * mm});
            skPoint(sketch, "E576.MirrorP", {"position": v(-29.37, -28.58) * mm});
            skPoint(sketch, "E577.MirrorP", {"position": v(-42.07, -28.57) * mm});
            skPoint(sketch, "E578.MirrorP", {"position": v(26.2, -28.58) * mm});
            skPoint(sketch, "E579.MirrorP", {"position": v(47.62, -11.9) * mm});
            skPoint(sketch, "E580.MirrorP", {"position": v(-11.9, -28.57) * mm});
            skPoint(sketch, "E581.MirrorP", {"position": v(-47.62, -26.2) * mm});
            skPoint(sketch, "E582.MirrorP", {"position": v(46.83, -26.2) * mm});
            skArc(sketch, "E583.MirrorCS", {"start": v(18.26, -28.58) * mm, "mid": v(15.88, -26.2) * mm, "end": v(13.5, -28.58) * mm});
            skPoint(sketch, "E584.MirrorP", {"position": v(23.02, -28.58) * mm});
            skPoint(sketch, "E585.MirrorP", {"position": v(40.48, -28.58) * mm});
            skCircle(sketch, "E586.MirrorC", {"center": v(49.21, -28.58) * mm, "radius": 1.2 * mm});
            skPoint(sketch, "E587.MirrorP", {"position": v(19.84, -28.58) * mm});
            skPoint(sketch, "E588.MirrorP", {"position": v(3.97, -28.57) * mm});
            skCircle(sketch, "E589.MirrorC", {"center": v(15.88, -28.57) * mm, "radius": 1.2 * mm});
            skPoint(sketch, "E590.MirrorP", {"position": v(47.62, -19.84) * mm});
            skPoint(sketch, "E591.MirrorP", {"position": v(11.9, -28.57) * mm});
            skPoint(sketch, "E592.MirrorP", {"position": v(47.62, -23.02) * mm});
            skPoint(sketch, "E593.MirrorP", {"position": v(0.8, -28.57) * mm});
            skPoint(sketch, "E594.MirrorP", {"position": v(47.62, -10.32) * mm});
            skPoint(sketch, "E595.MirrorP", {"position": v(43.66, -28.58) * mm});
            skPoint(sketch, "E596.MirrorP", {"position": v(47.62, -0.8) * mm});
            skPoint(sketch, "E597.MirrorP", {"position": v(38.9, -28.58) * mm});
            skPoint(sketch, "E598.MirrorP", {"position": v(-47.62, -0.8) * mm});
            skPoint(sketch, "E599.MirrorP", {"position": v(27.78, -28.58) * mm});
            skPoint(sketch, "E600.MirrorP", {"position": v(5.56, -28.57) * mm});
            skPoint(sketch, "E601.MirrorP", {"position": v(47.62, -13.5) * mm});
            skPoint(sketch, "E602.MirrorP", {"position": v(47.62, -21.43) * mm});
            skPoint(sketch, "E603.MirrorP", {"position": v(47.62, -3.97) * mm});
            skPoint(sketch, "E604.MirrorP", {"position": v(47.62, -8.73) * mm});
            skPoint(sketch, "E605.MirrorP", {"position": v(10.32, -28.57) * mm});
            skPoint(sketch, "E606.MirrorP", {"position": v(47.62, -2.38) * mm});
            skPoint(sketch, "E607.MirrorP", {"position": v(47.62, -26.2) * mm});
            skPoint(sketch, "E608.MirrorP", {"position": v(45.24, -28.57) * mm});
            skPoint(sketch, "E609.MirrorP", {"position": v(47.62, -15.08) * mm});
            skPoint(sketch, "E610.MirrorP", {"position": v(47.62, -16.67) * mm});
            skPoint(sketch, "E611.MirrorP", {"position": v(32.54, -28.58) * mm});
            skPoint(sketch, "E612.MirrorP", {"position": v(29.37, -28.58) * mm});
            skPoint(sketch, "E613.MirrorP", {"position": v(47.62, -7.14) * mm});
            skPoint(sketch, "E614.MirrorP", {"position": v(35.72, -28.58) * mm});
            skPoint(sketch, "E615.MirrorP", {"position": v(24.6, -28.58) * mm});
            skPoint(sketch, "E616.MirrorP", {"position": v(8.73, -28.57) * mm});
            skSolve(sketch);
        }
        {
            var Q0;
            Q0=makeQuery(id+"F0.imprint","IMPRINT",FACE,{"disambiguationData":[TD([[makeQuery(id+"F0.imprint","IMPRINT",EDGE,{"derivedFrom":sQuery(id+"F0.wireOp",EDGE,"E0.bottom")}),-1.0]])]});
            extrude(context, id + "F1", {"entities" : qUnion([Q0]), "endBound" : BoundingType.SYMMETRIC, "depth" : 155.57 * mm});
        }
        {
            var Q0;
            Q0=makeQuery(id+"F1.opExtrude","SWEPT_FACE",FACE,{"disambiguationData":[OSD([sQuery(id+"F0.wireOp",EDGE,"E0.right")])]});
            var sketch = newSketch(context, id + "F2", { "sketchPlane" : qUnion([Q0])});
            skLineSegment(sketch, "E617.bottom", {"start": v(-77.79, 32.54) * mm, "end": v(-76.2, 32.54) * mm});
            skLineSegment(sketch, "E617.top", {"start": v(-77.79, -32.54) * mm, "end": v(-76.2, -32.54) * mm});
            skLineSegment(sketch, "E617.left", {"start": v(-77.79, 32.54) * mm, "end": v(-77.79, -32.54) * mm});
            skLineSegment(sketch, "E617.right", {"start": v(-76.2, 32.54) * mm, "end": v(-76.2, -32.54) * mm});
            skLineSegment(sketch, "E618.MirrorCS", {"start": v(77.79, 32.54) * mm, "end": v(76.2, 32.54) * mm});
            skLineSegment(sketch, "E619.MirrorCS", {"start": v(77.79, -32.54) * mm, "end": v(76.2, -32.54) * mm});
            skLineSegment(sketch, "E620.MirrorCS", {"start": v(77.79, 32.54) * mm, "end": v(77.79, -32.54) * mm});
            skLineSegment(sketch, "E621.MirrorCS", {"start": v(76.2, 32.54) * mm, "end": v(76.2, -32.54) * mm});
            skSolve(sketch);
        }
        {
            var Q0;
            Q0 = qSketchRegion(id + "F2", true);
            var Q1;
            Q1=makeQuery(id+"F1.opExtrude","SWEPT_FACE",FACE,{"disambiguationData":[OSD([sQuery(id+"F0.wireOp",EDGE,"E0.left")])]});
            extrude(context, id + "F3", {"entities" : qUnion([Q0]), "operationType" : NewBodyOperationType.REMOVE, "endBound" : BoundingType.UP_TO_SURFACE, "oppositeDirection" : true, "endBoundEntityFace" : qUnion([Q1]), "depth" : 25.4 * mm});
        }
        {
            var Q0;
            Q0=makeQuery(id+"F1.opExtrude","SWEPT_FACE",FACE,{"disambiguationData":[OSD([sQuery(id+"F0.wireOp",EDGE,"E0.top")])]});
            var sketch = newSketch(context, id + "F4", { "sketchPlane" : qUnion([Q0])});
            skPoint(sketch, "E622", {"position": v(0, 0) * mm});
            skPoint(sketch, "E623", {"position": v(0, -25.4) * mm});
            skPoint(sketch, "E624", {"position": v(0, 25.4) * mm});
            skSolve(sketch);
        }
        {
            var Q0;
            Q0=sQuery(id+"F4.wireOp",VERTEX,"E624");
            var Q1;
            Q1=sQuery(id+"F4.wireOp",VERTEX,"E622");
            var Q2;
            Q2=sQuery(id+"F4.wireOp",VERTEX,"E623");
            var Q3;
            Q3=makeQuery(id+"F1.opExtrude","SWEPT_BODY",BODY,{"disambiguationData":[OSD([sQuery(id+"F0.wireOp",EDGE,"E0.bottom"),sQuery(id+"F0.wireOp",EDGE,"E0.top"),sQuery(id+"F0.wireOp",EDGE,"E0.left"),sQuery(id+"F0.wireOp",EDGE,"E1.bottom"),sQuery(id+"F0.wireOp",EDGE,"E1.top"),sQuery(id+"F0.wireOp",EDGE,"E1.left"),sQuery(id+"F0.wireOp",EDGE,"E2"),sQuery(id+"F0.wireOp",EDGE,"E3.bottom"),sQuery(id+"F0.wireOp",EDGE,"E3.top"),sQuery(id+"F0.wireOp",EDGE,"E3.left"),sQuery(id+"F0.wireOp",EDGE,"E4"),sQuery(id+"F0.wireOp",EDGE,"E5.bottom"),sQuery(id+"F0.wireOp",EDGE,"E5.top"),sQuery(id+"F0.wireOp",EDGE,"E5.left"),sQuery(id+"F0.wireOp",EDGE,"E6"),sQuery(id+"F0.wireOp",EDGE,"E7.bottom"),sQuery(id+"F0.wireOp",EDGE,"E7.top"),sQuery(id+"F0.wireOp",EDGE,"E7.left"),sQuery(id+"F0.wireOp",EDGE,"E8"),sQuery(id+"F0.wireOp",EDGE,"E9.bottom"),sQuery(id+"F0.wireOp",EDGE,"E9.top"),sQuery(id+"F0.wireOp",EDGE,"E9.left"),sQuery(id+"F0.wireOp",EDGE,"E10"),sQuery(id+"F0.wireOp",EDGE,"E11.bottom"),sQuery(id+"F0.wireOp",EDGE,"E11.top"),sQuery(id+"F0.wireOp",EDGE,"E11.left"),sQuery(id+"F0.wireOp",EDGE,"E12"),sQuery(id+"F0.wireOp",EDGE,"E13.bottom"),sQuery(id+"F0.wireOp",EDGE,"E13.top"),sQuery(id+"F0.wireOp",EDGE,"E13.left"),sQuery(id+"F0.wireOp",EDGE,"E14"),sQuery(id+"F0.wireOp",EDGE,"E15.bottom"),sQuery(id+"F0.wireOp",EDGE,"E15.left"),sQuery(id+"F0.wireOp",EDGE,"E16.bottom"),sQuery(id+"F0.wireOp",EDGE,"E16.top"),sQuery(id+"F0.wireOp",EDGE,"E16.left"),sQuery(id+"F0.wireOp",EDGE,"E17"),sQuery(id+"F0.wireOp",EDGE,"E18"),sQuery(id+"F0.wireOp",EDGE,"E19"),sQuery(id+"F0.wireOp",EDGE,"E20"),sQuery(id+"F0.wireOp",EDGE,"E21.filletArc"),sQuery(id+"F0.wireOp",EDGE,"E22.filletArc"),sQuery(id+"F0.wireOp",EDGE,"E23.filletArc"),sQuery(id+"F0.wireOp",EDGE,"E24.filletArc"),sQuery(id+"F0.wireOp",EDGE,"E25.filletArc"),sQuery(id+"F0.wireOp",EDGE,"E26.filletArc"),sQuery(id+"F0.wireOp",EDGE,"E27.filletArc"),sQuery(id+"F0.wireOp",EDGE,"E28.filletArc"),sQuery(id+"F0.wireOp",EDGE,"E29.filletArc"),sQuery(id+"F0.wireOp",EDGE,"E30.filletArc"),sQuery(id+"F0.wireOp",EDGE,"E31.filletArc"),sQuery(id+"F0.wireOp",EDGE,"E32.filletArc"),sQuery(id+"F0.wireOp",EDGE,"E33.filletArc"),sQuery(id+"F0.wireOp",EDGE,"E34.filletArc"),sQuery(id+"F0.wireOp",EDGE,"E35.filletArc"),sQuery(id+"F0.wireOp",EDGE,"E36.filletArc"),sQuery(id+"F0.wireOp",EDGE,"E37.top"),sQuery(id+"F0.wireOp",EDGE,"E37.left"),sQuery(id+"F0.wireOp",EDGE,"E38"),sQuery(id+"F0.wireOp",EDGE,"E39.filletArc"),sQuery(id+"F0.wireOp",EDGE,"E40.filletArc"),sQuery(id+"F0.wireOp",EDGE,"E41.bottom"),sQuery(id+"F0.wireOp",EDGE,"E42.top"),sQuery(id+"F0.wireOp",EDGE,"E42.left"),sQuery(id+"F0.wireOp",EDGE,"E43"),sQuery(id+"F0.wireOp",EDGE,"E44.filletArc"),sQuery(id+"F0.wireOp",EDGE,"E45.filletArc"),sQuery(id+"F0.wireOp",EDGE,"E46.bottom"),sQuery(id+"F0.wireOp",EDGE,"E47.top"),sQuery(id+"F0.wireOp",EDGE,"E47.left"),sQuery(id+"F0.wireOp",EDGE,"E48"),sQuery(id+"F0.wireOp",EDGE,"E49.filletArc"),sQuery(id+"F0.wireOp",EDGE,"E50.filletArc"),sQuery(id+"F0.wireOp",EDGE,"E51.bottom"),sQuery(id+"F0.wireOp",EDGE,"E52.top"),sQuery(id+"F0.wireOp",EDGE,"E52.left"),sQuery(id+"F0.wireOp",EDGE,"E53"),sQuery(id+"F0.wireOp",EDGE,"E54.filletArc"),sQuery(id+"F0.wireOp",EDGE,"E55.filletArc"),sQuery(id+"F0.wireOp",EDGE,"E56.bottom"),sQuery(id+"F0.wireOp",EDGE,"E57.top"),sQuery(id+"F0.wireOp",EDGE,"E57.left"),sQuery(id+"F0.wireOp",EDGE,"E58"),sQuery(id+"F0.wireOp",EDGE,"E59.filletArc"),sQuery(id+"F0.wireOp",EDGE,"E60.filletArc"),sQuery(id+"F0.wireOp",EDGE,"E61.bottom"),sQuery(id+"F0.wireOp",EDGE,"E62.top"),sQuery(id+"F0.wireOp",EDGE,"E62.left"),sQuery(id+"F0.wireOp",EDGE,"E63"),sQuery(id+"F0.wireOp",EDGE,"E64.filletArc"),sQuery(id+"F0.wireOp",EDGE,"E65.filletArc"),sQuery(id+"F0.wireOp",EDGE,"E66.bottom"),sQuery(id+"F0.wireOp",EDGE,"E67.top"),sQuery(id+"F0.wireOp",EDGE,"E67.left"),sQuery(id+"F0.wireOp",EDGE,"E68"),sQuery(id+"F0.wireOp",EDGE,"E69.filletArc"),sQuery(id+"F0.wireOp",EDGE,"E70.filletArc"),sQuery(id+"F0.wireOp",EDGE,"E71.bottom"),sQuery(id+"F0.wireOp",EDGE,"E72.top"),sQuery(id+"F0.wireOp",EDGE,"E72.left"),sQuery(id+"F0.wireOp",EDGE,"E73"),sQuery(id+"F0.wireOp",EDGE,"E74.filletArc"),sQuery(id+"F0.wireOp",EDGE,"E75.filletArc"),sQuery(id+"F0.wireOp",EDGE,"E76.bottom"),sQuery(id+"F0.wireOp",EDGE,"E77.top"),sQuery(id+"F0.wireOp",EDGE,"E77.left"),sQuery(id+"F0.wireOp",EDGE,"E78.bottom"),sQuery(id+"F0.wireOp",EDGE,"E79.top"),sQuery(id+"F0.wireOp",EDGE,"E79.left"),sQuery(id+"F0.wireOp",EDGE,"E80"),sQuery(id+"F0.wireOp",EDGE,"E81.filletArc"),sQuery(id+"F0.wireOp",EDGE,"E82.filletArc"),sQuery(id+"F0.wireOp",EDGE,"E83.bottom"),sQuery(id+"F0.wireOp",EDGE,"E84.top"),sQuery(id+"F0.wireOp",EDGE,"E84.left"),sQuery(id+"F0.wireOp",EDGE,"E85"),sQuery(id+"F0.wireOp",EDGE,"E86.filletArc"),sQuery(id+"F0.wireOp",EDGE,"E87.filletArc"),sQuery(id+"F0.wireOp",EDGE,"E88.bottom"),sQuery(id+"F0.wireOp",EDGE,"E89.top"),sQuery(id+"F0.wireOp",EDGE,"E89.left"),sQuery(id+"F0.wireOp",EDGE,"E90"),sQuery(id+"F0.wireOp",EDGE,"E91.filletArc"),sQuery(id+"F0.wireOp",EDGE,"E92.filletArc"),sQuery(id+"F0.wireOp",EDGE,"E93.bottom"),sQuery(id+"F0.wireOp",EDGE,"E94.top"),sQuery(id+"F0.wireOp",EDGE,"E95"),sQuery(id+"F0.wireOp",EDGE,"E96.filletArc"),sQuery(id+"F0.wireOp",EDGE,"E97.filletArc"),sQuery(id+"F0.wireOp",EDGE,"E98"),sQuery(id+"F0.wireOp",EDGE,"E0.right"),sQuery(id+"F0.wireOp",EDGE,"E99"),sQuery(id+"F0.wireOp",EDGE,"E101.filletArc"),sQuery(id+"F0.wireOp",EDGE,"E102.filletArc"),sQuery(id+"F0.wireOp",EDGE,"E103"),sQuery(id+"F0.wireOp",EDGE,"E104.MirrorCS"),sQuery(id+"F0.wireOp",EDGE,"E105.MirrorCS"),sQuery(id+"F0.wireOp",EDGE,"E106.MirrorCS"),sQuery(id+"F0.wireOp",EDGE,"E107.MirrorCS"),sQuery(id+"F0.wireOp",EDGE,"E108.MirrorCS"),sQuery(id+"F0.wireOp",EDGE,"E109.MirrorCS"),sQuery(id+"F0.wireOp",EDGE,"E110.MirrorCS"),sQuery(id+"F0.wireOp",EDGE,"E111.MirrorCS"),sQuery(id+"F0.wireOp",EDGE,"E112.MirrorCS"),sQuery(id+"F0.wireOp",EDGE,"E113.MirrorCS"),sQuery(id+"F0.wireOp",EDGE,"E114.MirrorCS"),sQuery(id+"F0.wireOp",EDGE,"E115.MirrorCS"),sQuery(id+"F0.wireOp",EDGE,"E116.MirrorCS"),sQuery(id+"F0.wireOp",EDGE,"E117.MirrorCS"),sQuery(id+"F0.wireOp",EDGE,"E118.MirrorCS"),sQuery(id+"F0.wireOp",EDGE,"E119.MirrorCS"),sQuery(id+"F0.wireOp",EDGE,"E120.MirrorCS"),sQuery(id+"F0.wireOp",EDGE,"E121.MirrorCS"),sQuery(id+"F0.wireOp",EDGE,"E122.MirrorCS"),sQuery(id+"F0.wireOp",EDGE,"E123.MirrorCS"),sQuery(id+"F0.wireOp",EDGE,"E124.MirrorCS"),sQuery(id+"F0.wireOp",EDGE,"E125.MirrorCS"),sQuery(id+"F0.wireOp",EDGE,"E126.MirrorCS"),sQuery(id+"F0.wireOp",EDGE,"E127.MirrorCS"),sQuery(id+"F0.wireOp",EDGE,"E128.MirrorCS"),sQuery(id+"F0.wireOp",EDGE,"E129.MirrorCS"),sQuery(id+"F0.wireOp",EDGE,"E130.MirrorCS"),sQuery(id+"F0.wireOp",EDGE,"E131.MirrorCS"),sQuery(id+"F0.wireOp",EDGE,"E132.MirrorCS"),sQuery(id+"F0.wireOp",EDGE,"E133.MirrorCS"),sQuery(id+"F0.wireOp",EDGE,"E134.MirrorCS"),sQuery(id+"F0.wireOp",EDGE,"E135.MirrorCS"),sQuery(id+"F0.wireOp",EDGE,"E136.MirrorCS"),sQuery(id+"F0.wireOp",EDGE,"E137.MirrorCS"),sQuery(id+"F0.wireOp",EDGE,"E138.MirrorCS"),sQuery(id+"F0.wireOp",EDGE,"E139.MirrorCS"),sQuery(id+"F0.wireOp",EDGE,"E140.MirrorCS"),sQuery(id+"F0.wireOp",EDGE,"E141.MirrorCS"),sQuery(id+"F0.wireOp",EDGE,"E142.MirrorCS"),sQuery(id+"F0.wireOp",EDGE,"E143.MirrorCS"),sQuery(id+"F0.wireOp",EDGE,"E144.MirrorCS"),sQuery(id+"F0.wireOp",EDGE,"E145.MirrorCS"),sQuery(id+"F0.wireOp",EDGE,"E146.MirrorCS"),sQuery(id+"F0.wireOp",EDGE,"E147.MirrorCS"),sQuery(id+"F0.wireOp",EDGE,"E148.MirrorCS"),sQuery(id+"F0.wireOp",EDGE,"E149.MirrorCS"),sQuery(id+"F0.wireOp",EDGE,"E150.MirrorCS"),sQuery(id+"F0.wireOp",EDGE,"E151.MirrorCS"),sQuery(id+"F0.wireOp",EDGE,"E152.MirrorCS"),sQuery(id+"F0.wireOp",EDGE,"E153.MirrorCS"),sQuery(id+"F0.wireOp",EDGE,"E154.MirrorCS"),sQuery(id+"F0.wireOp",EDGE,"E155.MirrorCS"),sQuery(id+"F0.wireOp",EDGE,"E156.MirrorCS"),sQuery(id+"F0.wireOp",EDGE,"E157.MirrorCS"),sQuery(id+"F0.wireOp",EDGE,"E158.MirrorCS"),sQuery(id+"F0.wireOp",EDGE,"E159.MirrorCS"),sQuery(id+"F0.wireOp",EDGE,"E160.MirrorCS"),sQuery(id+"F0.wireOp",EDGE,"E161.MirrorCS"),sQuery(id+"F0.wireOp",EDGE,"E162.MirrorCS"),sQuery(id+"F0.wireOp",EDGE,"E163.MirrorCS"),sQuery(id+"F0.wireOp",EDGE,"E164.MirrorCS"),sQuery(id+"F0.wireOp",EDGE,"E165.MirrorCS"),sQuery(id+"F0.wireOp",EDGE,"E166.MirrorCS"),sQuery(id+"F0.wireOp",EDGE,"E167.MirrorCS"),sQuery(id+"F0.wireOp",EDGE,"E168.MirrorCS"),sQuery(id+"F0.wireOp",EDGE,"E169.MirrorCS"),sQuery(id+"F0.wireOp",EDGE,"E170.MirrorCS"),sQuery(id+"F0.wireOp",EDGE,"E171.MirrorCS"),sQuery(id+"F0.wireOp",EDGE,"E172.MirrorCS"),sQuery(id+"F0.wireOp",EDGE,"E173.MirrorCS"),sQuery(id+"F0.wireOp",EDGE,"E174.MirrorCS"),sQuery(id+"F0.wireOp",EDGE,"E175.MirrorCS"),sQuery(id+"F0.wireOp",EDGE,"E176.MirrorCS"),sQuery(id+"F0.wireOp",EDGE,"E177.MirrorCS"),sQuery(id+"F0.wireOp",EDGE,"E178.MirrorCS"),sQuery(id+"F0.wireOp",EDGE,"E179.MirrorCS"),sQuery(id+"F0.wireOp",EDGE,"E180.MirrorCS"),sQuery(id+"F0.wireOp",EDGE,"E181.MirrorCS"),sQuery(id+"F0.wireOp",EDGE,"E182.MirrorCS"),sQuery(id+"F0.wireOp",EDGE,"E183.MirrorCS"),sQuery(id+"F0.wireOp",EDGE,"E184.MirrorCS"),sQuery(id+"F0.wireOp",EDGE,"E185.MirrorCS"),sQuery(id+"F0.wireOp",EDGE,"E186.MirrorCS"),sQuery(id+"F0.wireOp",EDGE,"E187.MirrorCS"),sQuery(id+"F0.wireOp",EDGE,"E188.MirrorCS"),sQuery(id+"F0.wireOp",EDGE,"E192.MirrorCS"),sQuery(id+"F0.wireOp",EDGE,"E194.MirrorCS"),sQuery(id+"F0.wireOp",EDGE,"E195.MirrorCS"),sQuery(id+"F0.wireOp",EDGE,"E196.MirrorCS"),sQuery(id+"F0.wireOp",EDGE,"E197.MirrorCS"),sQuery(id+"F0.wireOp",EDGE,"E201.MirrorCS"),sQuery(id+"F0.wireOp",EDGE,"E202.MirrorCS"),sQuery(id+"F0.wireOp",EDGE,"E204.MirrorCS"),sQuery(id+"F0.wireOp",EDGE,"E207.MirrorCS"),sQuery(id+"F0.wireOp",EDGE,"E212.MirrorCS"),sQuery(id+"F0.wireOp",EDGE,"E213.MirrorCS"),sQuery(id+"F0.wireOp",EDGE,"E214.MirrorCS"),sQuery(id+"F0.wireOp",EDGE,"E215.MirrorCS"),sQuery(id+"F0.wireOp",EDGE,"E220.MirrorCS"),sQuery(id+"F0.wireOp",EDGE,"E222.MirrorCS"),sQuery(id+"F0.wireOp",EDGE,"E223.MirrorCS"),sQuery(id+"F0.wireOp",EDGE,"E224.MirrorCS"),sQuery(id+"F0.wireOp",EDGE,"E226.MirrorCS"),sQuery(id+"F0.wireOp",EDGE,"E229.MirrorCS"),sQuery(id+"F0.wireOp",EDGE,"E230.MirrorCS"),sQuery(id+"F0.wireOp",EDGE,"E231.MirrorCS"),sQuery(id+"F0.wireOp",EDGE,"E233.MirrorCS"),sQuery(id+"F0.wireOp",EDGE,"E236.MirrorCS"),sQuery(id+"F0.wireOp",EDGE,"E237.MirrorCS"),sQuery(id+"F0.wireOp",EDGE,"E238.MirrorCS"),sQuery(id+"F0.wireOp",EDGE,"E240.MirrorCS"),sQuery(id+"F0.wireOp",EDGE,"E241.MirrorCS"),sQuery(id+"F0.wireOp",EDGE,"E242.MirrorCS"),sQuery(id+"F0.wireOp",EDGE,"E244.MirrorCS"),sQuery(id+"F0.wireOp",EDGE,"E246.MirrorCS"),sQuery(id+"F0.wireOp",EDGE,"E247.MirrorCS"),sQuery(id+"F0.wireOp",EDGE,"E248.MirrorCS"),sQuery(id+"F0.wireOp",EDGE,"E250.MirrorCS"),sQuery(id+"F0.wireOp",EDGE,"E251.MirrorCS"),sQuery(id+"F0.wireOp",EDGE,"E252.MirrorCS"),sQuery(id+"F0.wireOp",EDGE,"E253.MirrorCS"),sQuery(id+"F0.wireOp",EDGE,"E254.MirrorCS"),sQuery(id+"F0.wireOp",EDGE,"E262.MirrorCS"),sQuery(id+"F0.wireOp",EDGE,"E263.MirrorCS"),sQuery(id+"F0.wireOp",EDGE,"E264.MirrorCS"),sQuery(id+"F0.wireOp",EDGE,"E265.MirrorCS"),sQuery(id+"F0.wireOp",EDGE,"E266.MirrorCS"),sQuery(id+"F0.wireOp",EDGE,"E267.MirrorCS"),sQuery(id+"F0.wireOp",EDGE,"E271.MirrorC"),sQuery(id+"F0.wireOp",EDGE,"E273.MirrorCS"),sQuery(id+"F0.wireOp",EDGE,"E274.MirrorC"),sQuery(id+"F0.wireOp",EDGE,"E275.MirrorCS"),sQuery(id+"F0.wireOp",EDGE,"E276.MirrorCS"),sQuery(id+"F0.wireOp",EDGE,"E277.MirrorCS"),sQuery(id+"F0.wireOp",EDGE,"E278.MirrorCS"),sQuery(id+"F0.wireOp",EDGE,"E279.MirrorCS"),sQuery(id+"F0.wireOp",EDGE,"E280.MirrorCS"),sQuery(id+"F0.wireOp",EDGE,"E281.MirrorCS"),sQuery(id+"F0.wireOp",EDGE,"E282.MirrorCS"),sQuery(id+"F0.wireOp",EDGE,"E283.MirrorCS"),sQuery(id+"F0.wireOp",EDGE,"E284.MirrorCS"),sQuery(id+"F0.wireOp",EDGE,"E285.MirrorCS"),sQuery(id+"F0.wireOp",EDGE,"E286.MirrorCS"),sQuery(id+"F0.wireOp",EDGE,"E287.MirrorCS"),sQuery(id+"F0.wireOp",EDGE,"E288.MirrorCS"),sQuery(id+"F0.wireOp",EDGE,"E289.MirrorCS"),sQuery(id+"F0.wireOp",EDGE,"E290.MirrorCS"),sQuery(id+"F0.wireOp",EDGE,"E291.MirrorCS"),sQuery(id+"F0.wireOp",EDGE,"E292.MirrorCS"),sQuery(id+"F0.wireOp",EDGE,"E293.MirrorCS"),sQuery(id+"F0.wireOp",EDGE,"E294.MirrorCS"),sQuery(id+"F0.wireOp",EDGE,"E295.MirrorCS"),sQuery(id+"F0.wireOp",EDGE,"E296.MirrorCS"),sQuery(id+"F0.wireOp",EDGE,"E297.MirrorCS"),sQuery(id+"F0.wireOp",EDGE,"E298.MirrorCS"),sQuery(id+"F0.wireOp",EDGE,"E299.MirrorCS"),sQuery(id+"F0.wireOp",EDGE,"E300.MirrorCS"),sQuery(id+"F0.wireOp",EDGE,"E301.MirrorCS"),sQuery(id+"F0.wireOp",EDGE,"E302.MirrorCS"),sQuery(id+"F0.wireOp",EDGE,"E303.MirrorCS"),sQuery(id+"F0.wireOp",EDGE,"E304.MirrorCS"),sQuery(id+"F0.wireOp",EDGE,"E305.MirrorCS"),sQuery(id+"F0.wireOp",EDGE,"E306.MirrorCS"),sQuery(id+"F0.wireOp",EDGE,"E307.MirrorCS"),sQuery(id+"F0.wireOp",EDGE,"E308.MirrorCS"),sQuery(id+"F0.wireOp",EDGE,"E309.MirrorCS"),sQuery(id+"F0.wireOp",EDGE,"E310.MirrorCS"),sQuery(id+"F0.wireOp",EDGE,"E311.MirrorCS"),sQuery(id+"F0.wireOp",EDGE,"E312.MirrorCS"),sQuery(id+"F0.wireOp",EDGE,"E313.MirrorCS"),sQuery(id+"F0.wireOp",EDGE,"E314.MirrorCS"),sQuery(id+"F0.wireOp",EDGE,"E315.MirrorCS"),sQuery(id+"F0.wireOp",EDGE,"E316.MirrorCS"),sQuery(id+"F0.wireOp",EDGE,"E317.MirrorCS"),sQuery(id+"F0.wireOp",EDGE,"E318.MirrorCS"),sQuery(id+"F0.wireOp",EDGE,"E319.MirrorCS"),sQuery(id+"F0.wireOp",EDGE,"E320.MirrorCS"),sQuery(id+"F0.wireOp",EDGE,"E321.MirrorCS"),sQuery(id+"F0.wireOp",EDGE,"E322.MirrorCS"),sQuery(id+"F0.wireOp",EDGE,"E323.MirrorCS"),sQuery(id+"F0.wireOp",EDGE,"E324.MirrorCS"),sQuery(id+"F0.wireOp",EDGE,"E325.MirrorCS"),sQuery(id+"F0.wireOp",EDGE,"E326.MirrorCS"),sQuery(id+"F0.wireOp",EDGE,"E327.MirrorCS"),sQuery(id+"F0.wireOp",EDGE,"E328.MirrorCS"),sQuery(id+"F0.wireOp",EDGE,"E329.MirrorCS"),sQuery(id+"F0.wireOp",EDGE,"E330.MirrorCS"),sQuery(id+"F0.wireOp",EDGE,"E331.MirrorCS"),sQuery(id+"F0.wireOp",EDGE,"E332.MirrorCS"),sQuery(id+"F0.wireOp",EDGE,"E333.MirrorCS"),sQuery(id+"F0.wireOp",EDGE,"E334.MirrorCS"),sQuery(id+"F0.wireOp",EDGE,"E335.MirrorCS"),sQuery(id+"F0.wireOp",EDGE,"E336.MirrorCS"),sQuery(id+"F0.wireOp",EDGE,"E337.MirrorCS"),sQuery(id+"F0.wireOp",EDGE,"E338.MirrorCS"),sQuery(id+"F0.wireOp",EDGE,"E339.MirrorCS"),sQuery(id+"F0.wireOp",EDGE,"E340.MirrorCS"),sQuery(id+"F0.wireOp",EDGE,"E341.MirrorCS"),sQuery(id+"F0.wireOp",EDGE,"E342.MirrorCS"),sQuery(id+"F0.wireOp",EDGE,"E343.MirrorCS"),sQuery(id+"F0.wireOp",EDGE,"E344.MirrorCS"),sQuery(id+"F0.wireOp",EDGE,"E345.MirrorCS"),sQuery(id+"F0.wireOp",EDGE,"E346.MirrorCS"),sQuery(id+"F0.wireOp",EDGE,"E347.MirrorCS"),sQuery(id+"F0.wireOp",EDGE,"E348.MirrorCS"),sQuery(id+"F0.wireOp",EDGE,"E349.MirrorCS"),sQuery(id+"F0.wireOp",EDGE,"E350.MirrorCS"),sQuery(id+"F0.wireOp",EDGE,"E351.MirrorCS"),sQuery(id+"F0.wireOp",EDGE,"E352.MirrorCS"),sQuery(id+"F0.wireOp",EDGE,"E353.MirrorCS"),sQuery(id+"F0.wireOp",EDGE,"E354.MirrorCS"),sQuery(id+"F0.wireOp",EDGE,"E355.MirrorCS"),sQuery(id+"F0.wireOp",EDGE,"E356.MirrorCS"),sQuery(id+"F0.wireOp",EDGE,"E357.MirrorCS"),sQuery(id+"F0.wireOp",EDGE,"E358.MirrorCS"),sQuery(id+"F0.wireOp",EDGE,"E359.MirrorCS"),sQuery(id+"F0.wireOp",EDGE,"E360.MirrorCS"),sQuery(id+"F0.wireOp",EDGE,"E361.MirrorCS"),sQuery(id+"F0.wireOp",EDGE,"E362.MirrorCS"),sQuery(id+"F0.wireOp",EDGE,"E363.MirrorCS"),sQuery(id+"F0.wireOp",EDGE,"E364.MirrorCS"),sQuery(id+"F0.wireOp",EDGE,"E365.MirrorCS"),sQuery(id+"F0.wireOp",EDGE,"E366.MirrorCS"),sQuery(id+"F0.wireOp",EDGE,"E367.MirrorCS"),sQuery(id+"F0.wireOp",EDGE,"E368.MirrorCS"),sQuery(id+"F0.wireOp",EDGE,"E369.MirrorCS"),sQuery(id+"F0.wireOp",EDGE,"E370.MirrorCS"),sQuery(id+"F0.wireOp",EDGE,"E371.MirrorCS"),sQuery(id+"F0.wireOp",EDGE,"E372.MirrorCS"),sQuery(id+"F0.wireOp",EDGE,"E373.MirrorCS"),sQuery(id+"F0.wireOp",EDGE,"E374.MirrorCS"),sQuery(id+"F0.wireOp",EDGE,"E375.MirrorCS"),sQuery(id+"F0.wireOp",EDGE,"E376.MirrorCS"),sQuery(id+"F0.wireOp",EDGE,"E377.MirrorCS"),sQuery(id+"F0.wireOp",EDGE,"E378.MirrorCS"),sQuery(id+"F0.wireOp",EDGE,"E379.MirrorCS"),sQuery(id+"F0.wireOp",EDGE,"E380.MirrorCS"),sQuery(id+"F0.wireOp",EDGE,"E381.MirrorCS"),sQuery(id+"F0.wireOp",EDGE,"E382.MirrorCS"),sQuery(id+"F0.wireOp",EDGE,"E383.MirrorCS"),sQuery(id+"F0.wireOp",EDGE,"E384.MirrorCS"),sQuery(id+"F0.wireOp",EDGE,"E385.MirrorCS"),sQuery(id+"F0.wireOp",EDGE,"E386.MirrorCS"),sQuery(id+"F0.wireOp",EDGE,"E387.MirrorCS"),sQuery(id+"F0.wireOp",EDGE,"E388.MirrorCS"),sQuery(id+"F0.wireOp",EDGE,"E389.MirrorCS"),sQuery(id+"F0.wireOp",EDGE,"E390.MirrorCS"),sQuery(id+"F0.wireOp",EDGE,"E391.MirrorCS"),sQuery(id+"F0.wireOp",EDGE,"E392.MirrorCS"),sQuery(id+"F0.wireOp",EDGE,"E393.MirrorCS"),sQuery(id+"F0.wireOp",EDGE,"E394.MirrorCS"),sQuery(id+"F0.wireOp",EDGE,"E395.MirrorCS"),sQuery(id+"F0.wireOp",EDGE,"E396.MirrorCS"),sQuery(id+"F0.wireOp",EDGE,"E397.MirrorCS"),sQuery(id+"F0.wireOp",EDGE,"E398.MirrorCS"),sQuery(id+"F0.wireOp",EDGE,"E399.MirrorCS"),sQuery(id+"F0.wireOp",EDGE,"E400.MirrorCS"),sQuery(id+"F0.wireOp",EDGE,"E401.MirrorCS"),sQuery(id+"F0.wireOp",EDGE,"E402.MirrorCS"),sQuery(id+"F0.wireOp",EDGE,"E403.MirrorCS"),sQuery(id+"F0.wireOp",EDGE,"E404.MirrorCS"),sQuery(id+"F0.wireOp",EDGE,"E405.MirrorCS"),sQuery(id+"F0.wireOp",EDGE,"E406.MirrorCS"),sQuery(id+"F0.wireOp",EDGE,"E407.MirrorCS"),sQuery(id+"F0.wireOp",EDGE,"E408.MirrorCS"),sQuery(id+"F0.wireOp",EDGE,"E409.MirrorCS"),sQuery(id+"F0.wireOp",EDGE,"E410.MirrorCS"),sQuery(id+"F0.wireOp",EDGE,"E411.MirrorCS"),sQuery(id+"F0.wireOp",EDGE,"E412.MirrorCS"),sQuery(id+"F0.wireOp",EDGE,"E413.MirrorCS"),sQuery(id+"F0.wireOp",EDGE,"E414.MirrorCS"),sQuery(id+"F0.wireOp",EDGE,"E415.MirrorCS"),sQuery(id+"F0.wireOp",EDGE,"E416.MirrorCS"),sQuery(id+"F0.wireOp",EDGE,"E417.MirrorCS"),sQuery(id+"F0.wireOp",EDGE,"E418.MirrorCS"),sQuery(id+"F0.wireOp",EDGE,"E419.MirrorCS"),sQuery(id+"F0.wireOp",EDGE,"E420.MirrorCS"),sQuery(id+"F0.wireOp",EDGE,"E421.MirrorCS"),sQuery(id+"F0.wireOp",EDGE,"E422.MirrorCS"),sQuery(id+"F0.wireOp",EDGE,"E423.MirrorCS"),sQuery(id+"F0.wireOp",EDGE,"E424.MirrorCS"),sQuery(id+"F0.wireOp",EDGE,"E425.MirrorCS"),sQuery(id+"F0.wireOp",EDGE,"E426.MirrorCS"),sQuery(id+"F0.wireOp",EDGE,"E427.MirrorCS"),sQuery(id+"F0.wireOp",EDGE,"E428.MirrorCS"),sQuery(id+"F0.wireOp",EDGE,"E429.MirrorCS"),sQuery(id+"F0.wireOp",EDGE,"E430.MirrorCS"),sQuery(id+"F0.wireOp",EDGE,"E431.MirrorCS"),sQuery(id+"F0.wireOp",EDGE,"E432.MirrorCS"),sQuery(id+"F0.wireOp",EDGE,"E433.MirrorCS"),sQuery(id+"F0.wireOp",EDGE,"E434.MirrorCS"),sQuery(id+"F0.wireOp",EDGE,"E435.MirrorCS"),sQuery(id+"F0.wireOp",EDGE,"E436.MirrorCS"),sQuery(id+"F0.wireOp",EDGE,"E437.MirrorCS"),sQuery(id+"F0.wireOp",EDGE,"E438.MirrorCS"),sQuery(id+"F0.wireOp",EDGE,"E439.MirrorCS"),sQuery(id+"F0.wireOp",EDGE,"E440.MirrorCS"),sQuery(id+"F0.wireOp",EDGE,"E441.MirrorCS"),sQuery(id+"F0.wireOp",EDGE,"E442.MirrorCS"),sQuery(id+"F0.wireOp",EDGE,"E443.MirrorCS"),sQuery(id+"F0.wireOp",EDGE,"E444.MirrorCS"),sQuery(id+"F0.wireOp",EDGE,"E445.MirrorCS"),sQuery(id+"F0.wireOp",EDGE,"E446.MirrorCS"),sQuery(id+"F0.wireOp",EDGE,"E447.MirrorCS"),sQuery(id+"F0.wireOp",EDGE,"E448.MirrorCS"),sQuery(id+"F0.wireOp",EDGE,"E449.MirrorCS"),sQuery(id+"F0.wireOp",EDGE,"E450.MirrorCS"),sQuery(id+"F0.wireOp",EDGE,"E451.MirrorCS"),sQuery(id+"F0.wireOp",EDGE,"E452.MirrorCS"),sQuery(id+"F0.wireOp",EDGE,"E453.MirrorCS"),sQuery(id+"F0.wireOp",EDGE,"E454.MirrorCS"),sQuery(id+"F0.wireOp",EDGE,"E455.MirrorCS"),sQuery(id+"F0.wireOp",EDGE,"E456.MirrorCS"),sQuery(id+"F0.wireOp",EDGE,"E457.MirrorCS"),sQuery(id+"F0.wireOp",EDGE,"E458.MirrorCS"),sQuery(id+"F0.wireOp",EDGE,"E459.MirrorCS"),sQuery(id+"F0.wireOp",EDGE,"E460.MirrorCS"),sQuery(id+"F0.wireOp",EDGE,"E461.MirrorCS"),sQuery(id+"F0.wireOp",EDGE,"E462.MirrorCS"),sQuery(id+"F0.wireOp",EDGE,"E463.MirrorCS"),sQuery(id+"F0.wireOp",EDGE,"E464.MirrorCS"),sQuery(id+"F0.wireOp",EDGE,"E465.MirrorCS"),sQuery(id+"F0.wireOp",EDGE,"E467.MirrorCS"),sQuery(id+"F0.wireOp",EDGE,"E468.MirrorCS"),sQuery(id+"F0.wireOp",EDGE,"E469.MirrorCS"),sQuery(id+"F0.wireOp",EDGE,"E470.MirrorCS"),sQuery(id+"F0.wireOp",EDGE,"E472.MirrorCS"),sQuery(id+"F0.wireOp",EDGE,"E473.MirrorCS"),sQuery(id+"F0.wireOp",EDGE,"E474.MirrorCS"),sQuery(id+"F0.wireOp",EDGE,"E475.MirrorCS"),sQuery(id+"F0.wireOp",EDGE,"E476.MirrorCS"),sQuery(id+"F0.wireOp",EDGE,"E478.MirrorCS"),sQuery(id+"F0.wireOp",EDGE,"E479.MirrorCS"),sQuery(id+"F0.wireOp",EDGE,"E480.MirrorCS"),sQuery(id+"F0.wireOp",EDGE,"E481.MirrorCS"),sQuery(id+"F0.wireOp",EDGE,"E482.MirrorCS"),sQuery(id+"F0.wireOp",EDGE,"E483.MirrorCS"),sQuery(id+"F0.wireOp",EDGE,"E484.MirrorCS"),sQuery(id+"F0.wireOp",EDGE,"E485.MirrorCS"),sQuery(id+"F0.wireOp",EDGE,"E486.MirrorCS"),sQuery(id+"F0.wireOp",EDGE,"E487.MirrorCS"),sQuery(id+"F0.wireOp",EDGE,"E488.MirrorCS"),sQuery(id+"F0.wireOp",EDGE,"E489.MirrorCS"),sQuery(id+"F0.wireOp",EDGE,"E490.MirrorCS"),sQuery(id+"F0.wireOp",EDGE,"E492.MirrorCS"),sQuery(id+"F0.wireOp",EDGE,"E493.MirrorCS"),sQuery(id+"F0.wireOp",EDGE,"E494.MirrorCS"),sQuery(id+"F0.wireOp",EDGE,"E495.MirrorCS"),sQuery(id+"F0.wireOp",EDGE,"E496.MirrorCS"),sQuery(id+"F0.wireOp",EDGE,"E497.MirrorCS"),sQuery(id+"F0.wireOp",EDGE,"E498.MirrorCS"),sQuery(id+"F0.wireOp",EDGE,"E499.MirrorCS"),sQuery(id+"F0.wireOp",EDGE,"E500.MirrorCS"),sQuery(id+"F0.wireOp",EDGE,"E501.MirrorCS"),sQuery(id+"F0.wireOp",EDGE,"E502.MirrorCS"),sQuery(id+"F0.wireOp",EDGE,"E503.MirrorCS"),sQuery(id+"F0.wireOp",EDGE,"E504.MirrorCS"),sQuery(id+"F0.wireOp",EDGE,"E505.MirrorCS"),sQuery(id+"F0.wireOp",EDGE,"E506.MirrorCS"),sQuery(id+"F0.wireOp",EDGE,"E508.MirrorCS"),sQuery(id+"F0.wireOp",EDGE,"E509.MirrorCS"),sQuery(id+"F0.wireOp",EDGE,"E510.MirrorCS"),sQuery(id+"F0.wireOp",EDGE,"E511.MirrorCS"),sQuery(id+"F0.wireOp",EDGE,"E512.MirrorCS"),sQuery(id+"F0.wireOp",EDGE,"E513.MirrorCS"),sQuery(id+"F0.wireOp",EDGE,"E514.MirrorCS"),sQuery(id+"F0.wireOp",EDGE,"E515.MirrorCS"),sQuery(id+"F0.wireOp",EDGE,"E516.MirrorCS"),sQuery(id+"F0.wireOp",EDGE,"E517.MirrorCS"),sQuery(id+"F0.wireOp",EDGE,"E518.MirrorCS"),sQuery(id+"F0.wireOp",EDGE,"E519.MirrorCS"),sQuery(id+"F0.wireOp",EDGE,"E520.MirrorCS"),sQuery(id+"F0.wireOp",EDGE,"E521.MirrorCS"),sQuery(id+"F0.wireOp",EDGE,"E522.MirrorCS"),sQuery(id+"F0.wireOp",EDGE,"E523.MirrorCS"),sQuery(id+"F0.wireOp",EDGE,"E524.MirrorCS"),sQuery(id+"F0.wireOp",EDGE,"E525.MirrorCS"),sQuery(id+"F0.wireOp",EDGE,"E527.MirrorCS"),sQuery(id+"F0.wireOp",EDGE,"E528.MirrorCS"),sQuery(id+"F0.wireOp",EDGE,"E529.MirrorCS"),sQuery(id+"F0.wireOp",EDGE,"E530.MirrorCS"),sQuery(id+"F0.wireOp",EDGE,"E532.MirrorCS"),sQuery(id+"F0.wireOp",EDGE,"E534.MirrorCS"),sQuery(id+"F0.wireOp",EDGE,"E535.MirrorCS"),sQuery(id+"F0.wireOp",EDGE,"E536.MirrorCS"),sQuery(id+"F0.wireOp",EDGE,"E537.MirrorCS"),sQuery(id+"F0.wireOp",EDGE,"E538.MirrorCS"),sQuery(id+"F0.wireOp",EDGE,"E543.MirrorC"),sQuery(id+"F0.wireOp",EDGE,"E550.MirrorCS"),sQuery(id+"F0.wireOp",EDGE,"E554.MirrorC"),sQuery(id+"F0.wireOp",EDGE,"E583.MirrorCS"),sQuery(id+"F0.wireOp",EDGE,"E586.MirrorC"),sQuery(id+"F0.wireOp",EDGE,"E589.MirrorC")])]});
            hole(context, id + "F5", {"style" : HoleStyle.SIMPLE, "endStyle" : HoleEndStyle.BLIND, "standardTappedOrClearance" : lookupTablePath({ "standard" : "ANSI", "engagement" : "75%", "pitch" : "24 tpi", "size" : "3/8", "type" : "Tapped" }), "standardBlindInLast" : lookupTablePath({ "standard" : "ANSI", "engagement" : "75%", "pitch" : "24 tpi", "size" : "3/8", "type" : "Tapped" }), "holeDiameter" : 8.43 * mm, "holeDepth" : 12.7 * mm, "locations" : qUnion([Q0, Q1, Q2]), "scope" : qUnion([Q3]), "tappedDepth" : 12.7 * mm, "tapClearance" : 3, "majorDiameter" : 9.53 * mm});
        }
    });
